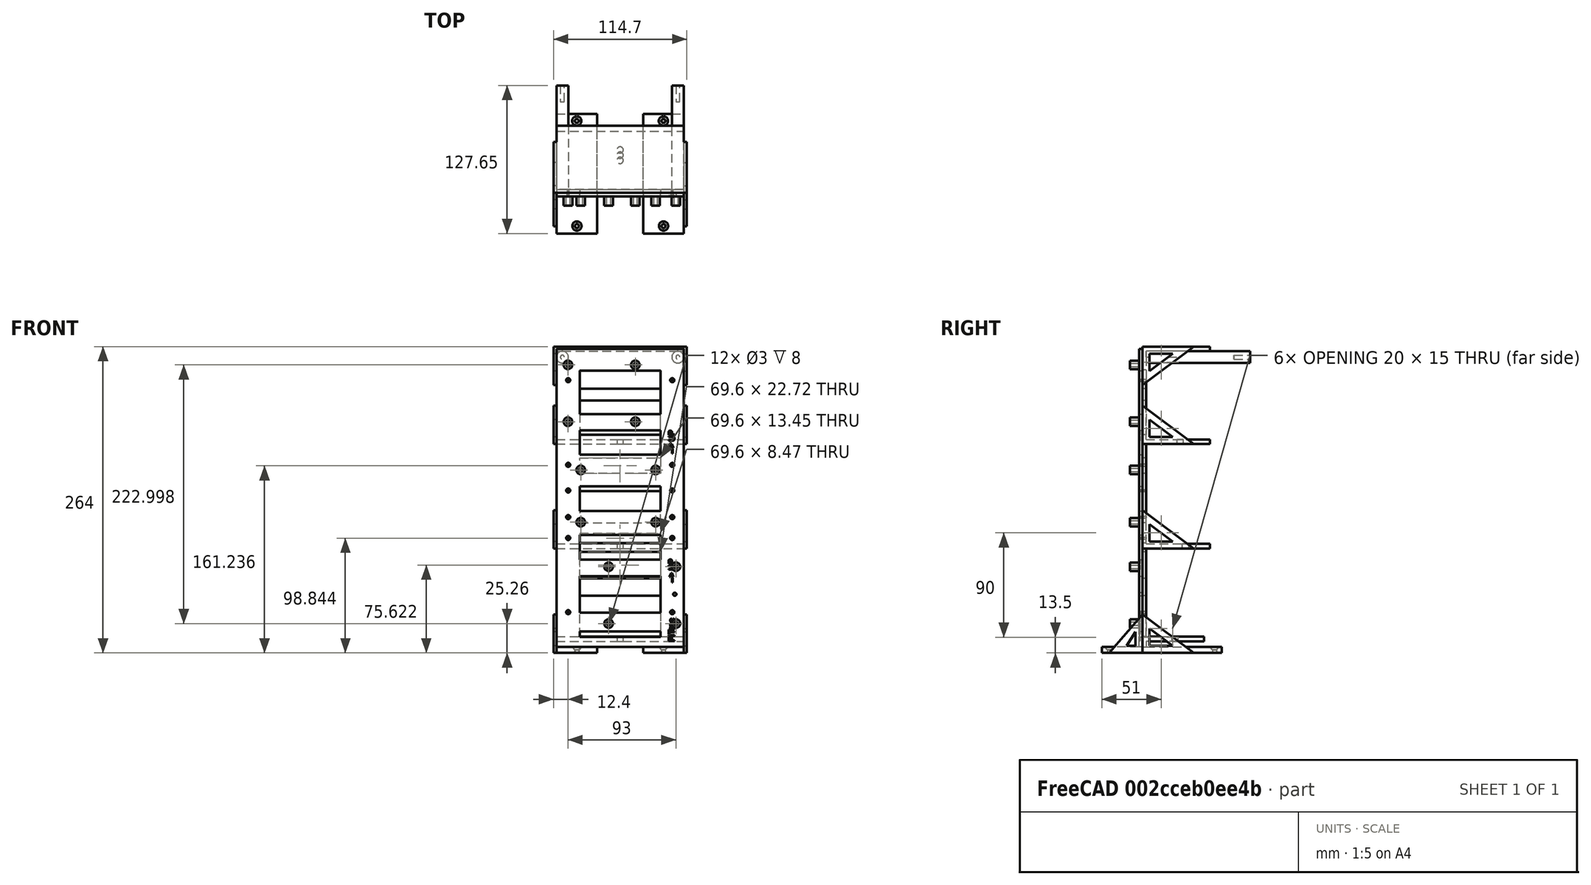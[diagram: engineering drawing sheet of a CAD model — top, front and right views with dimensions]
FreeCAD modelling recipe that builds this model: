
FCSTD DOCUMENT  (FreeCAD 1.0R39109 (Git))
Label: Tower
License: All rights reserved
LicenseURL: http://en.wikipedia.org/wiki/All_rights_reserved
objects: Sketcher::SketchObject×17, PartDesign::Pad×9, PartDesign::Plane×9, PartDesign::Pocket×5, PartDesign::Hole×3, PartDesign::Mirrored×2, PartDesign::Body×2, App::Link×1, Part::Part2DObjectPython×1, App::Part×1
note: 101 computed .brp shape members not serialized (recipe doc carries the construction recipe); baked Part::Feature solids carry a one-line shape summary decoded from their .brp
EXTERNAL_REF file=../Master Document.FCStd obj=Spreadsheet

FEATURE [App::Link] Link  label="Monitor Chassis Parameters"
  LinkedObject = -> <external ../Master Document.FCStd>#Spreadsheet
FEATURE [Sketcher::SketchObject] Sketch  label="Backplate Sketch"
  ArcFitTolerance = 1e-06
  AttachmentSupport = -> [XZ_Plane001]
  FullyConstrained = false
  MakeInternals = false
  MapMode = 5
  Placement = pos=(0,0,0) rot=(1,0,0;1.5708rad)
  expr: Constraints[10] = <<Monitor Chassis Parameters>>.GSBackPlateBoltDiameter
  expr: Constraints[11] = <<Monitor Chassis Parameters>>.GSComputeBoardWidth / 2 - <<Monitor Chassis Parameters>>.GSBackPlateOuterHolesInsetFromSide
  expr: Constraints[15] = <<Monitor Chassis Parameters>>.GSBackPlateWidthIncrement
  expr: Constraints[55] = <<Monitor Chassis Parameters>>.GSBackPlateLengthIncrement
  expr: Constraints[59] = <<Monitor Chassis Parameters>>.GSBackPlateWidth
  expr: Constraints[71] = <<Monitor Chassis Parameters>>.GSBackPlateMinimumSpanWidth
  expr: Constraints[72] = <<Monitor Chassis Parameters>>.GSBackPlateMinimumSpanWidth
  expr: Constraints[7] = <<Monitor Chassis Parameters>>.GSComputeBoardHeight
  expr: Constraints[80] = <<Monitor Chassis Parameters>>.GSBackPlateLengthIncrement
  expr: Constraints[8] = <<Monitor Chassis Parameters>>.GSComputeBoardWidth
  expr: Constraints[9] = <<Monitor Chassis Parameters>>.GSComputeBoardWidth / 2
  sketch-geometry (37):
    g0: LineSegment [constr] StartX=-50.8 StartY=24.4067 StartZ=0 EndX=50.8 EndY=24.4067 EndZ=0
    g1: LineSegment [constr] StartX=50.8 StartY=24.4067 StartZ=0 EndX=50.8 EndY=253.007 EndZ=0
    g2: LineSegment [constr] StartX=50.8 StartY=253.007 StartZ=0 EndX=-50.8 EndY=253.007 EndZ=0
    g3: LineSegment [constr] StartX=-50.8 StartY=253.007 StartZ=0 EndX=-50.8 EndY=24.4067 EndZ=0
    g4: Circle CenterX=46.99 CenterY=45.5 CenterZ=0 NormalX=0 NormalY=0 NormalZ=1 AngleXU=0 Radius=1.4
    g5: LineSegment StartX=-54.8 StartY=257.007 StartZ=0 EndX=-54.8 EndY=20.4067 EndZ=0
    g6: LineSegment [constr] StartX=-54.8 StartY=20.4067 StartZ=0 EndX=54.8 EndY=20.4067 EndZ=0
    g7: LineSegment StartX=34.8 StartY=117.208 StartZ=0 EndX=-34.8 EndY=117.208 EndZ=0
    g8: LineSegment StartX=-34.8 StartY=117.208 StartZ=0 EndX=-34.8 EndY=138.47 EndZ=0
    g9: LineSegment StartX=-34.8 StartY=138.47 StartZ=0 EndX=34.8 EndY=138.47 EndZ=0
    g10: LineSegment StartX=34.8 StartY=138.47 StartZ=0 EndX=34.8 EndY=117.208 EndZ=0
    g11: LineSegment StartX=34.8 StartY=238.176 StartZ=0 EndX=-34.8 EndY=238.176 EndZ=0
    g12: LineSegment StartX=-34.8 StartY=238.176 StartZ=0 EndX=-34.8 EndY=200.906 EndZ=0
    g13: LineSegment StartX=-34.8 StartY=200.906 StartZ=0 EndX=34.8 EndY=200.906 EndZ=0
    g14: LineSegment StartX=34.8 StartY=200.906 StartZ=0 EndX=34.8 EndY=238.176 EndZ=0
    g15: LineSegment StartX=-34.8 StartY=186.911 StartZ=0 EndX=-34.8 EndY=165.729 EndZ=0
    g16: LineSegment StartX=-34.8 StartY=165.729 StartZ=0 EndX=34.8 EndY=165.729 EndZ=0
    g17: LineSegment StartX=34.8 StartY=165.729 StartZ=0 EndX=34.8 EndY=186.911 EndZ=0
    g18: LineSegment StartX=34.8 StartY=186.911 StartZ=0 EndX=-34.8 EndY=186.911 EndZ=0
    g19: LineSegment StartX=-34.8 StartY=96.4911 StartZ=0 EndX=-34.8 EndY=75.4807 EndZ=0
    g20: LineSegment StartX=-34.8 StartY=75.4807 StartZ=0 EndX=34.8 EndY=75.4807 EndZ=0
    g21: LineSegment StartX=34.8 StartY=75.4807 StartZ=0 EndX=34.8 EndY=96.4911 EndZ=0
    g22: LineSegment StartX=34.8 StartY=96.4911 StartZ=0 EndX=-34.8 EndY=96.4911 EndZ=0
    g23: LineSegment StartX=-34.8 StartY=61.1974 StartZ=0 EndX=-34.8 EndY=29.6985 EndZ=0
    g24: LineSegment StartX=34.8 StartY=29.6985 StartZ=0 EndX=34.8 EndY=61.1974 EndZ=0
    g25: LineSegment StartX=54.8 StartY=20.4067 StartZ=0 EndX=54.8 EndY=257.007 EndZ=0
    g26: LineSegment StartX=-54.8 StartY=257.007 StartZ=0 EndX=54.8 EndY=257.007 EndZ=0
    g27: LineSegment StartX=-54.8 StartY=20.4067 StartZ=0 EndX=-54.8 EndY=0 EndZ=0
    g28: LineSegment StartX=-54.8 StartY=0 StartZ=0 EndX=54.8 EndY=0 EndZ=0
    g29: LineSegment StartX=54.8 StartY=0 StartZ=0 EndX=54.8 EndY=20.4067 EndZ=0
    g30: LineSegment [constr] StartX=54.8 StartY=20.4067 StartZ=0 EndX=-54.8 EndY=20.4067 EndZ=0
    g31: LineSegment StartX=-34.8 StartY=61.1974 StartZ=0 EndX=34.8 EndY=61.1974 EndZ=0
    g32: LineSegment StartX=-34.8 StartY=29.6985 StartZ=0 EndX=34.8 EndY=29.6985 EndZ=0
    g33: LineSegment StartX=-34.8 StartY=13.3729 StartZ=0 EndX=-34.8 EndY=8.79995 EndZ=0
    g34: LineSegment StartX=-34.8 StartY=8.79995 StartZ=0 EndX=34.8 EndY=8.79995 EndZ=0
    g35: LineSegment StartX=34.8 StartY=8.79995 StartZ=0 EndX=34.8 EndY=13.3729 EndZ=0
    g36: LineSegment StartX=34.8 StartY=13.3729 StartZ=0 EndX=-34.8 EndY=13.3729 EndZ=0
  constraints (96):
    c: Coincident(g0,g1)
    c: Coincident(g1,g2)
    c: Coincident(g2,g3)
    c: Coincident(g3,g0)
    c: Horizontal(g2)
    c: Vertical(g1)
    c: Vertical(g3)
    c: DistanceY(g0,g2) = 228.6
    c: DistanceX(g0,g0) = 101.6
    c: DistanceX(g0,g-1) = 50.8
    c: Diameter(g4) = 2.8
    c: DistanceX(g-1,g4) = 46.99
    c: Coincident(g5,g6)
    c: Vertical(g5)
    c: Horizontal(g6)
    c: DistanceX(g5,g0) = 4
    c: Horizontal(g0)
    c: Coincident(g7,g8)
    c: Coincident(g8,g9)
    c: Coincident(g9,g10)
    c: Coincident(g10,g7)
    c: Horizontal(g7)
    c: Vertical(g8)
    c: Vertical(g10)
    c: Coincident(g11,g12)
    c: Coincident(g12,g13)
    c: Coincident(g13,g14)
    c: Coincident(g14,g11)
    c: Horizontal(g11)
    c: Horizontal(g13)
    c: Vertical(g12)
    c: Vertical(g14)
    c: Coincident(g15,g16)
    c: Coincident(g16,g17)
    c: Coincident(g17,g18)
    c: Coincident(g18,g15)
    c: Vertical(g15)
    c: Vertical(g17)
    c: Horizontal(g16)
    c: Coincident(g19,g20)
    c: Coincident(g20,g21)
    c: Coincident(g21,g22)
    c: Coincident(g22,g19)
    c: Vertical(g19)
    c: Vertical(g21)
    c: Horizontal(g20)
    c: Horizontal(g22)
    c: Vertical(g23)
    c: Vertical(g24)
    c: Vertical(g15,g19)
    c: Vertical(g19,g23)
    c: Vertical(g7,g21)
    c: Vertical(g21,g24)
    c: Coincident(g25,g6)
    c: Vertical(g25)
    c: DistanceY(g1,g25) = 4
    c: Horizontal(g5,g25)
    c: Coincident(g26,g5)
    c: Coincident(g26,g25)
    c: DistanceX(g5,g6) = 109.6
    c: Coincident(g27,g28)
    c: Coincident(g28,g29)
    c: Coincident(g29,g30)
    c: Coincident(g30,g27)
    c: Vertical(g27)
    c: Vertical(g29)
    c: Horizontal(g28)
    c: Horizontal(g30)
    c: Coincident(g27,g5)
    c: Horizontal(g28,g-1)
    c: Vertical(g29,g6)
    c: DistanceX(g5,g11) = 20
    c: DistanceX(g11,g25) = 20
    c: Horizontal(g9)
    c: Coincident(g31,g23)
    c: Coincident(g31,g24)
    c: Horizontal(g31)
    c: Vertical(g11,g15)
    c: Vertical(g11,g9)
    c: Vertical(g16,g9)
    c: DistanceY(g5,g0) = 4
    c: Coincident(g32,g23)
    c: Coincident(g32,g24)
    c: Horizontal(g32)
    c: Horizontal(g18)
    c: Vertical(g15,g8)
    c: Coincident(g33,g34)
    c: Coincident(g34,g35)
    c: Coincident(g35,g36)
    c: Coincident(g36,g33)
    c: Vertical(g33)
    c: Vertical(g35)
    c: Horizontal(g34)
    c: Horizontal(g36)
    c: Vertical(g23,g33)
    c: Vertical(g24,g35)
FEATURE [PartDesign::Pad] Pad  label="Backplate Pad"
  Direction = (0,-1,2e-16)
  Length = 3
  Length2 = 10
  Placement = pos=(0,0,0) rot=(1,0,0;1.5708rad)
  Profile = -> Sketch
  ReferenceAxis = -> Sketch [N_Axis]
  Reversed = true
  Suppressed = false
  Type = 0
  expr: Length = <<Monitor Chassis Parameters>>.GSBackPlateThickness
FEATURE [Sketcher::SketchObject] Sketch001  label="Backplate Risers Sketch"
  ArcFitTolerance = 1e-06
  AttachmentSupport = -> [XZ_Plane001]
  FullyConstrained = false
  MakeInternals = false
  MapMode = 5
  Placement = pos=(0,0,0) rot=(1,0,0;1.5708rad)
  expr: Constraints[10] = <<Monitor Chassis Parameters>>.GsPi5MountingHoleDiameter
  expr: Constraints[11] = <<Monitor Chassis Parameters>>.GsPi5MountingHoleDiameter
  expr: Constraints[12] = <<Monitor Chassis Parameters>>.GsPi5MountingHoleDiameter
  expr: Constraints[13] = <<Monitor Chassis Parameters>>.GsPi5MountingHoleDiameter
  expr: Constraints[17] = <<Monitor Chassis Parameters>>.GSBackPlateScrewHoleDiameter + 2 * <<Monitor Chassis Parameters>>.GSBackPlateStandoffWallThickness
  expr: Constraints[19] = <<Monitor Chassis Parameters>>.GSBackPlateScrewHoleDiameter + 2 * <<Monitor Chassis Parameters>>.GSBackPlateStandoffWallThickness
  expr: Constraints[25] = <<Monitor Chassis Parameters>>.GSBackPlateScrewHoleDiameter + 2 * <<Monitor Chassis Parameters>>.GSBackPlateStandoffWallThickness
  expr: Constraints[26] = <<Monitor Chassis Parameters>>.GSBackPlateScrewHoleDiameter + 2 * <<Monitor Chassis Parameters>>.GSBackPlateStandoffWallThickness
  expr: Constraints[27] = <<Monitor Chassis Parameters>>.GSBackPlateScrewHoleDiameter + 2 * <<Monitor Chassis Parameters>>.GSBackPlateStandoffWallThickness
  expr: Constraints[28] = <<Monitor Chassis Parameters>>.GSBackPlateScrewHoleDiameter + 2 * <<Monitor Chassis Parameters>>.GSBackPlateStandoffWallThickness
  expr: Constraints[29] = <<Monitor Chassis Parameters>>.GSBackPlateScrewHoleDiameter + 2 * <<Monitor Chassis Parameters>>.GSBackPlateStandoffWallThickness
  expr: Constraints[31] = <<Monitor Chassis Parameters>>.GSBackPlateVerticalOffset
  expr: Constraints[33] = <<Monitor Chassis Parameters>>.GSPi5MountingHoleCenterLength
  expr: Constraints[35] = <<Monitor Chassis Parameters>>.GSPi5MountingHoleCenterWidth
  expr: Constraints[37] = <<Monitor Chassis Parameters>>.GSPi5MountingHoleCenterWidth
  expr: Constraints[40] = <<Monitor Chassis Parameters>>.GsPi5MountingHoleDiameter
  expr: Constraints[57] = <<Monitor Chassis Parameters>>.GSMonitorConnectorBoardHoleSeparationLength
  expr: Constraints[58] = <<Monitor Chassis Parameters>>.GSMonitorConnectorBoardHoleSeparationWidth
  expr: Constraints[59] = 34
  expr: Constraints[60] = <<Monitor Chassis Parameters>>.GSPi5MountingHoleCenterLength
  expr: Constraints[61] = 10
  expr: Constraints[6] = <<Monitor Chassis Parameters>>.GSComputeBoardWidth / 2
  expr: Constraints[7] = <<Monitor Chassis Parameters>>.GsPi5MountingHoleDiameter
  expr: Constraints[8] = <<Monitor Chassis Parameters>>.GsPi5MountingHoleDiameter
  expr: Constraints[9] = <<Monitor Chassis Parameters>>.GsPi5MountingHoleDiameter
  sketch-geometry (28):
    g0: LineSegment [constr] StartX=-50.8 StartY=20 StartZ=0 EndX=50.8 EndY=20 EndZ=0
    g1: LineSegment [constr] StartX=50.8 StartY=20 StartZ=0 EndX=50.8 EndY=248.6 EndZ=0
    g2: LineSegment [constr] StartX=50.8 StartY=248.6 StartZ=0 EndX=-50.8 EndY=248.6 EndZ=0
    g3: LineSegment [constr] StartX=-50.8 StartY=248.6 StartZ=0 EndX=-50.8 EndY=20 EndZ=0
    g4: Circle CenterX=-45 CenterY=243.258 CenterZ=0 NormalX=0 NormalY=0 NormalZ=1 AngleXU=0 Radius=1.5
    g5: Circle CenterX=13 CenterY=243.258 CenterZ=0 NormalX=0 NormalY=0 NormalZ=1 AngleXU=0 Radius=1.5
    g6: Circle CenterX=-10 CenterY=20.2601 CenterZ=0 NormalX=0 NormalY=0 NormalZ=1 AngleXU=0 Radius=1.5
    g7: Circle CenterX=48 CenterY=20.2601 CenterZ=0 NormalX=0 NormalY=0 NormalZ=1 AngleXU=0 Radius=1.5
    g8: Circle CenterX=-10 CenterY=69.2601 CenterZ=0 NormalX=0 NormalY=0 NormalZ=1 AngleXU=0 Radius=1.5
    g9: Circle CenterX=-45 CenterY=194.258 CenterZ=0 NormalX=0 NormalY=0 NormalZ=1 AngleXU=0 Radius=1.5
    g10: Circle CenterX=13 CenterY=194.258 CenterZ=0 NormalX=0 NormalY=0 NormalZ=1 AngleXU=0 Radius=1.5
    g11: Circle CenterX=-45 CenterY=243.258 CenterZ=0 NormalX=0 NormalY=0 NormalZ=1 AngleXU=0 Radius=3.7
    g12: Circle CenterX=13 CenterY=243.258 CenterZ=0 NormalX=0 NormalY=0 NormalZ=1 AngleXU=0 Radius=3.7
    g13: Circle CenterX=-45 CenterY=194.258 CenterZ=0 NormalX=0 NormalY=0 NormalZ=1 AngleXU=0 Radius=3.7
    g14: Circle CenterX=13 CenterY=194.258 CenterZ=0 NormalX=0 NormalY=0 NormalZ=1 AngleXU=0 Radius=3.7
    g15: Circle CenterX=-10 CenterY=69.2601 CenterZ=0 NormalX=0 NormalY=0 NormalZ=1 AngleXU=0 Radius=3.7
    g16: Circle CenterX=-10 CenterY=20.2601 CenterZ=0 NormalX=0 NormalY=0 NormalZ=1 AngleXU=0 Radius=3.7
    g17: Circle CenterX=48 CenterY=20.2601 CenterZ=0 NormalX=0 NormalY=0 NormalZ=1 AngleXU=0 Radius=3.7
    g18: Circle CenterX=48 CenterY=69.2601 CenterZ=0 NormalX=0 NormalY=0 NormalZ=1 AngleXU=0 Radius=3.7
    g19: Circle CenterX=48 CenterY=69.2601 CenterZ=0 NormalX=0 NormalY=0 NormalZ=1 AngleXU=0 Radius=1.5
    g20: Circle CenterX=-34 CenterY=107.639 CenterZ=0 NormalX=0 NormalY=0 NormalZ=1 AngleXU=0 Radius=1.5
    g21: Circle CenterX=-34 CenterY=107.639 CenterZ=0 NormalX=0 NormalY=0 NormalZ=1 AngleXU=0 Radius=3.7
    g22: Circle CenterX=30.5 CenterY=107.639 CenterZ=0 NormalX=0 NormalY=0 NormalZ=1 AngleXU=0 Radius=1.5
    g23: Circle CenterX=30.5 CenterY=107.639 CenterZ=0 NormalX=0 NormalY=0 NormalZ=1 AngleXU=0 Radius=3.7
    g24: Circle CenterX=30.5 CenterY=152.639 CenterZ=0 NormalX=0 NormalY=0 NormalZ=1 AngleXU=0 Radius=1.5
    g25: Circle CenterX=30.5 CenterY=152.639 CenterZ=0 NormalX=0 NormalY=0 NormalZ=1 AngleXU=0 Radius=3.7
    g26: Circle CenterX=-34 CenterY=152.639 CenterZ=0 NormalX=0 NormalY=0 NormalZ=1 AngleXU=0 Radius=1.5
    g27: Circle CenterX=-34 CenterY=152.639 CenterZ=0 NormalX=0 NormalY=0 NormalZ=1 AngleXU=0 Radius=3.7
  constraints (67):
    c: Coincident(g0,g1)
    c: Coincident(g1,g2)
    c: Coincident(g2,g3)
    c: Coincident(g3,g0)
    c: Vertical(g1)
    c: Vertical(g3)
    c: DistanceX(g0,g-1) = 50.8
    c: Diameter(g4) = 3
    c: Diameter(g5) = 3
    c: Diameter(g6) = 3
    c: Diameter(g7) = 3
    c: Diameter(g8) = 3
    c: Diameter(g9) = 3
    c: Diameter(g10) = 3
    c: Horizontal(g0)
    c: Horizontal(g5,g4)
    c: Coincident(g11,g4)
    c: Diameter(g11) = 7.4
    c: Coincident(g12,g5)
    c: Diameter(g12) = 7.4
    c: Coincident(g13,g9)
    c: Coincident(g14,g10)
    c: Coincident(g15,g8)
    c: Coincident(g16,g6)
    c: Coincident(g17,g7)
    c: Diameter(g17) = 7.4
    c: Diameter(g16) = 7.4
    c: Diameter(g15) = 7.4
    c: Diameter(g14) = 7.4
    c: Diameter(g13) = 7.4
    c: Horizontal(g7,g6)
    c: DistanceY(g-1,g0) = 20
    c: Horizontal(g2,g1)
    c: DistanceX(g4,g5) = 58
    c: Horizontal(g9,g10)
    c: DistanceY(g9,g4) = 49
    c: Vertical(g8,g6)
    c: DistanceY(g6,g8) = 49
    c: Diameter(g18) = 7.4
    c: Coincident(g19,g18)
    c: Diameter(g19) = 3
    c: Horizontal(g18,g8)
    c: Vertical(g18,g7)
    c: Coincident(g21,g20)
    c: Diameter(g21) = 7.4
    c: Diameter(g20) = 3
    c: Coincident(g23,g22)
    c: Diameter(g23) = 7.4
    c: Diameter(g22) = 3
    c: Coincident(g25,g24)
    c: Diameter(g25) = 7.4
    c: Diameter(g24) = 3
    c: Coincident(g27,g26)
    c: Diameter(g27) = 7.4
    c: Diameter(g26) = 3
    c: Horizontal(g24,g26)
    c: Horizontal(g22,g20)
    c: DistanceX(g26,g24) = 64.5
    c: DistanceY(g20,g26) = 45
    c: DistanceX(g26,g-1) = 34
    c: DistanceX(g8,g18) = 58
    c: DistanceX(g6,g-1) = 10
    c: DistanceX(g9,g-1) = 45
    c: Vertical(g5,g10)
    c: Vertical(g4,g9)
    c: Vertical(g20,g26)
    c: Vertical(g24,g22)
FEATURE [PartDesign::Pad] Pad001  label="Backplate Risers Pad"
  BaseFeature = -> Pad
  Direction = (0,-1,2e-16)
  Length = 8
  Length2 = 10
  Placement = pos=(0,0,0) rot=(1,0,0;1.5708rad)
  Profile = -> Sketch001
  ReferenceAxis = -> Sketch001 [N_Axis]
  Suppressed = false
  Type = 0
  expr: Length = <<Monitor Chassis Parameters>>.GSBackPlateConnectorBoardVariantStandoffHeight
FEATURE [Sketcher::SketchObject] Sketch002  label="Backplate Foot Sketch"
  ArcFitTolerance = 1e-06
  AttachmentSupport = -> [XZ_Plane001]
  FullyConstrained = true
  MakeInternals = false
  MapMode = 5
  Placement = pos=(0,0,0) rot=(1,0,0;1.5708rad)
  expr: Constraints[11] = <<Monitor Chassis Parameters>>.GSTowerFeetThickness
  expr: Constraints[21] = <<Monitor Chassis Parameters>>.GSTowerFeetThickness
  expr: Constraints[22] = <<Monitor Chassis Parameters>>.GSBackPlateFootWidth
  expr: Constraints[23] = 0.5 * <<Monitor Chassis Parameters>>.GSBackPlateWidth
  expr: Constraints[8] = <<Monitor Chassis Parameters>>.GSBackPlateFootWidth
  expr: Constraints[9] = 0.5 * <<Monitor Chassis Parameters>>.GSBackPlateWidth
  sketch-geometry (8):
    g0: LineSegment StartX=-54.8 StartY=-5 StartZ=0 EndX=-19.8 EndY=-5 EndZ=0
    g1: LineSegment StartX=-19.8 StartY=-5 StartZ=0 EndX=-19.8 EndY=0 EndZ=0
    g2: LineSegment StartX=-19.8 StartY=0 StartZ=0 EndX=-54.8 EndY=0 EndZ=0
    g3: LineSegment StartX=-54.8 StartY=0 StartZ=0 EndX=-54.8 EndY=-5 EndZ=0
    g4: LineSegment StartX=54.8 StartY=-5 StartZ=0 EndX=54.8 EndY=0 EndZ=0
    g5: LineSegment StartX=54.8 StartY=0 StartZ=0 EndX=19.8 EndY=0 EndZ=0
    g6: LineSegment StartX=19.8 StartY=0 StartZ=0 EndX=19.8 EndY=-5 EndZ=0
    g7: LineSegment StartX=19.8 StartY=-5 StartZ=0 EndX=54.8 EndY=-5 EndZ=0
  constraints (24):
    c: Coincident(g0,g1)
    c: Coincident(g1,g2)
    c: Coincident(g2,g3)
    c: Coincident(g3,g0)
    c: Horizontal(g0)
    c: Horizontal(g2)
    c: Vertical(g1)
    c: Vertical(g3)
    c: DistanceX(g2,g1) = 35
    c: DistanceX(g2,g-1) = 54.8
    c: Horizontal(g2,g-1)
    c: DistanceY(g0,g2) = 5
    c: Coincident(g4,g5)
    c: Coincident(g5,g6)
    c: Coincident(g6,g7)
    c: Coincident(g7,g4)
    c: Vertical(g4)
    c: Vertical(g6)
    c: Horizontal(g5)
    c: Horizontal(g7)
    c: Horizontal(g5,g-1)
    c: DistanceY(g4,g4) = 5
    c: DistanceX(g6,g4) = 35
    c: DistanceX(g-1,g4) = 54.8
FEATURE [PartDesign::Pad] Pad002  label="Backplate Foot Pad"
  BaseFeature = -> Pad001
  Direction = (0,-1,2e-16)
  Length = 32
  Length2 = 3
  Placement = pos=(0,0,0) rot=(1,0,0;1.5708rad)
  Profile = -> Sketch002
  ReferenceAxis = -> Sketch002 [N_Axis]
  Suppressed = false
  Type = 4
  expr: Length = <<Monitor Chassis Parameters>>.GSBackPlateFootLengthBackward
  expr: Length2 = <<Monitor Chassis Parameters>>.GSBackPlateThickness
FEATURE [Sketcher::SketchObject] Sketch003  label="Backplate Foot Screw Holes Sketch"
  ArcFitTolerance = 1e-06
  AttachmentSupport = -> [XY_Plane001]
  FullyConstrained = true
  MakeInternals = false
  MapMode = 5
  expr: Constraints[0] = 0.8 * <<Monitor Chassis Parameters>>.GSBackPlateFootLengthBackward
  expr: Constraints[1] = 0.5 * <<Monitor Chassis Parameters>>.GSBackPlateWidth - 0.5 * <<Monitor Chassis Parameters>>.GSBackPlateFootWidth
  expr: Constraints[2] = 0.5 * <<Monitor Chassis Parameters>>.GSBackPlateWidth - 0.5 * <<Monitor Chassis Parameters>>.GSBackPlateFootWidth
  expr: Constraints[3] = <<Monitor Chassis Parameters>>.GSTowerFeetScrewDiameter
  expr: Constraints[4] = <<Monitor Chassis Parameters>>.GSTowerFeetScrewDiameter
  sketch-geometry (2):
    g0: Circle CenterX=-37.3 CenterY=-25.6 CenterZ=0 NormalX=0 NormalY=0 NormalZ=1 AngleXU=0 Radius=1.7
    g1: Circle CenterX=37.3 CenterY=-25.6 CenterZ=0 NormalX=0 NormalY=0 NormalZ=1 AngleXU=0 Radius=1.7
  constraints (6):
    c: DistanceY(g0,g-1) = 25.6
    c: DistanceX(g0,g-1) = 37.3
    c: DistanceX(g-1,g1) = 37.3
    c: Diameter(g0) = 3.4
    c: Diameter(g1) = 3.4
    c: Horizontal(g1,g0)
FEATURE [PartDesign::Hole] Hole  label="Backplate Foot Screw Holes"
  BaseFeature = -> Pad002
  CustomThreadClearance = 0
  Depth = 25
  DepthType = 0
  Diameter = 3.4
  DrillForDepth = false
  DrillPoint = 1
  DrillPointAngle = 118
  HoleCutCountersinkAngle = 90
  HoleCutCustomValues = false
  HoleCutDepth = 0
  HoleCutDiameter = 8
  HoleCutType = 2
  ModelThread = false
  Placement = pos=(0,0,0) rot=(1,0,0;1.5708rad)
  Profile = -> Sketch003
  Suppressed = false
  Tapered = false
  TaperedAngle = 90
  ThreadClass = 0
  ThreadDepth = 25
  ThreadDepthType = 0
  ThreadDirection = 0
  ThreadFit = 0
  ThreadSize = 0
  ThreadType = 0
  Threaded = false
  UseCustomThreadClearance = false
  expr: Diameter = <<Monitor Chassis Parameters>>.GSTowerFeetScrewDiameter
  expr: HoleCutDiameter = <<Monitor Chassis Parameters>>.GSM4BoltCountersinkDiameter
FEATURE [PartDesign::Plane] DatumPlane
  AttachmentOffset = pos=(0,0,54.8) rot=(0,0,1;0rad)
  AttachmentSupport = -> [YZ_Plane001]
  Length = 76.5738
  MapMode = 5
  Placement = pos=(54.8,0,0) rot=(0.57735,0.57735,0.57735;2.0944rad)
  ResizeMode = 0
  Width = 306.293
  expr: .AttachmentOffset.Base.z = 0.5 * <<Monitor Chassis Parameters>>.GSBackPlateWidth
FEATURE [Sketcher::SketchObject] Sketch004  label="Foot Support Corner Sketch"
  ArcFitTolerance = 1e-06
  AttachmentSupport = -> [DatumPlane]
  FullyConstrained = true
  MakeInternals = false
  MapMode = 5
  Placement = pos=(54.8,0,0) rot=(0.57735,0.57735,0.57735;2.0944rad)
  expr: Constraints[14] = <<Monitor Chassis Parameters>>.GSSideCornerCutoutInset
  expr: Constraints[15] = <<Monitor Chassis Parameters>>.GSSideCornerCutoutInset
  expr: Constraints[16] = 2.5 * <<Monitor Chassis Parameters>>.GSSideCornerCutoutInset
  expr: Constraints[17] = 2.5 * <<Monitor Chassis Parameters>>.GSSideCornerCutoutInset
  expr: Constraints[1] = <<Monitor Chassis Parameters>>.GSBackPlateThickness
  expr: Constraints[4] = <<Monitor Chassis Parameters>>.GSTowerFeetThickness
  expr: Constraints[7] = 0.9 * <<Monitor Chassis Parameters>>.GSBackPlateFootLengthBackward
  expr: Constraints[8] = 0.6 * <<Monitor Chassis Parameters>>.GSTowerFloorDepth
  sketch-geometry (6):
    g0: LineSegment StartX=-25.8 StartY=-5 StartZ=0 EndX=3 EndY=-5 EndZ=0
    g1: LineSegment StartX=3 StartY=28 StartZ=0 EndX=3 EndY=-5 EndZ=0
    g2: LineSegment StartX=-25.8 StartY=-5 StartZ=0 EndX=3 EndY=28 EndZ=0
    g3: LineSegment StartX=-10.8 StartY=1 StartZ=0 EndX=-3 EndY=13 EndZ=0
    g4: LineSegment StartX=-3 StartY=13 StartZ=0 EndX=-3 EndY=1 EndZ=0
    g5: LineSegment StartX=-10.8 StartY=1 StartZ=0 EndX=-3 EndY=1 EndZ=0
  constraints (18):
    c: Horizontal(g0)
    c: DistanceX(g-1,g0) = 3
    c: Coincident(g1,g0)
    c: Vertical(g1)
    c: DistanceY(g0,g-1) = 5
    c: Coincident(g2,g0)
    c: Coincident(g2,g1)
    c: DistanceX(g0,g0) = 28.8
    c: DistanceY(g0,g1) = 33
    c: Coincident(g4,g3)
    c: Vertical(g4)
    c: Coincident(g5,g3)
    c: Coincident(g5,g4)
    c: Horizontal(g5)
    c: DistanceY(g0,g4) = 6
    c: DistanceX(g4,g0) = 6
    c: DistanceX(g0,g3) = 15
    c: DistanceY(g3,g1) = 15
FEATURE [PartDesign::Pad] Pad003  label="Foot Support Corner Pad"
  BaseFeature = -> Hole
  Direction = (1,0,0)
  Length = 2.5
  Length2 = 10
  Placement = pos=(0,0,0) rot=(1,0,0;1.5708rad)
  Profile = -> Sketch004
  ReferenceAxis = -> Sketch004 [N_Axis]
  Suppressed = false
  Type = 0
  expr: Length = <<Monitor Chassis Parameters>>.GSSideCornerThickness
FEATURE [PartDesign::Mirrored] Mirrored  label="Foot Support Corner Mirrored"
  BaseFeature = -> Pad003
  MirrorPlane = -> YZ_Plane001
  Originals = -> [Pad003]
  Placement = pos=(0,0,0) rot=(1,0,0;1.5708rad)
  Suppressed = false
  TransformMode = 0
FEATURE [PartDesign::Plane] DatumPlane001
  AttachmentOffset = pos=(0,0,54.8) rot=(0,0,1;0rad)
  AttachmentSupport = -> [YZ_Plane002]
  Length = 121.975
  MapMode = 5
  Placement = pos=(54.8,0,0) rot=(0.57735,0.57735,0.57735;2.0944rad)
  ResizeMode = 0
  Width = 315.975
  expr: .AttachmentOffset.Base.z = 0.5 * <<Monitor Chassis Parameters>>.GSBackPlateWidth
FEATURE [Sketcher::SketchObject] Sketch005  label="Frontplate Sketch"
  ArcFitTolerance = 1e-06
  AttachmentSupport = -> [XZ_Plane002]
  FullyConstrained = false
  MakeInternals = false
  MapMode = 5
  Placement = pos=(0,0,0) rot=(1,0,0;1.5708rad)
  expr: Constraints[105] = <<Monitor Chassis Parameters>>.GSFrontPlateMinimumSpanWidth - 5
  expr: Constraints[106] = <<Monitor Chassis Parameters>>.GSTowerFourthFloorHeight + <<Monitor Chassis Parameters>>.GSTowerFloorThickness
  expr: Constraints[107] = <<Monitor Chassis Parameters>>.GSTowerLayerJoinScrewDiameter
  expr: Constraints[108] = <<Monitor Chassis Parameters>>.GSTowerLayerJoinScrewDiameter
  expr: Constraints[110] = <<Monitor Chassis Parameters>>.GSTowerLayerJoinScrewInset
  expr: Constraints[111] = <<Monitor Chassis Parameters>>.GSTowerLayerJoinScrewInset
  expr: Constraints[112] = <<Monitor Chassis Parameters>>.GSTowerLayerJoinScrewDiameter
  expr: Constraints[113] = <<Monitor Chassis Parameters>>.GSTowerLayerJoinScrewDiameter
  expr: Constraints[115] = <<Monitor Chassis Parameters>>.GSTowerLayerJoinScrewDiameter
  expr: Constraints[116] = <<Monitor Chassis Parameters>>.GSTowerLayerJoinScrewDiameter
  expr: Constraints[120] = <<Monitor Chassis Parameters>>.GSTowerLayerJoinScrewDiameter
  expr: Constraints[121] = <<Monitor Chassis Parameters>>.GSTowerLayerJoinScrewDiameter
  expr: Constraints[123] = <<Monitor Chassis Parameters>>.GSTowerLayerJoinScrewHeightFromFoot_1
  expr: Constraints[124] = <<Monitor Chassis Parameters>>.GSTowerLayerJoinScrewHeightFromFoot_3
  expr: Constraints[126] = <<Monitor Chassis Parameters>>.GSTowerLayerJoinScrewHeightFromFoot_4
  expr: Constraints[127] = <<Monitor Chassis Parameters>>.GSTowerLayerJoinScrewHeightFromFoot_5
  expr: Constraints[129] = <<Monitor Chassis Parameters>>.GSTowerLayerJoinScrewDiameter
  expr: Constraints[130] = <<Monitor Chassis Parameters>>.GSTowerLayerJoinScrewDiameter
  expr: Constraints[133] = <<Monitor Chassis Parameters>>.GSTowerLayerJoinScrewHeightFromFoot_6
  expr: Constraints[13] = <<Monitor Chassis Parameters>>.GSBackPlateWidthIncrement
  expr: Constraints[145] = <<Monitor Chassis Parameters>>.GSTowerLayerJoinScrewDiameter
  expr: Constraints[150] = <<Monitor Chassis Parameters>>.GSTowerLayerJoinScrewHeightFromFoot_2
  expr: Constraints[46] = <<Monitor Chassis Parameters>>.GSFrontPlateMinimumSpanWidth - 10
  expr: Constraints[48] = <<Monitor Chassis Parameters>>.GSFrontPlateMinimumSpanWidth
  expr: Constraints[65] = <<Monitor Chassis Parameters>>.GSFrontPlateMinimumSpanWidth - 5
  expr: Constraints[71] = <<Monitor Chassis Parameters>>.GSBackPlateLengthIncrement
  expr: Constraints[75] = <<Monitor Chassis Parameters>>.GSBackPlateWidth
  expr: Constraints[76] = <<Monitor Chassis Parameters>>.GSBackPlateVerticalOffset
  expr: Constraints[7] = <<Monitor Chassis Parameters>>.GSComputeBoardHeight
  expr: Constraints[8] = <<Monitor Chassis Parameters>>.GSComputeBoardWidth
  expr: Constraints[96] = <<Monitor Chassis Parameters>>.GSFrontPlateMinimumSpanWidth - 11
  expr: Constraints[97] = <<Monitor Chassis Parameters>>.GSFrontPlateMinimumSpanWidth
  expr: Constraints[98] = <<Monitor Chassis Parameters>>.GSFrontPlateMinimumSpanWidth
  expr: Constraints[9] = <<Monitor Chassis Parameters>>.GSComputeBoardWidth / 2
  sketch-geometry (55):
    g0: LineSegment [constr] StartX=-50.8 StartY=24 StartZ=0 EndX=50.8 EndY=24 EndZ=0
    g1: LineSegment [constr] StartX=50.8 StartY=24 StartZ=0 EndX=50.8 EndY=252.6 EndZ=0
    g2: LineSegment [constr] StartX=50.8 StartY=252.6 StartZ=0 EndX=-50.8 EndY=252.6 EndZ=0
    g3: LineSegment [constr] StartX=-50.8 StartY=252.6 StartZ=0 EndX=-50.8 EndY=24 EndZ=0
    g4: LineSegment StartX=-54.8 StartY=256.6 StartZ=0 EndX=-54.8 EndY=20 EndZ=0
    g5: LineSegment [constr] StartX=-54.8 StartY=20 StartZ=0 EndX=54.8 EndY=20 EndZ=0
    g6: LineSegment StartX=34.8 StartY=162.959 StartZ=0 EndX=-34.8 EndY=162.959 EndZ=0
    g7: LineSegment StartX=-34.8 StartY=162.959 StartZ=0 EndX=-34.8 EndY=149.512 EndZ=0
    g8: LineSegment StartX=-34.8 StartY=149.512 StartZ=0 EndX=34.8 EndY=149.512 EndZ=0
    g9: LineSegment StartX=34.8 StartY=149.512 StartZ=0 EndX=34.8 EndY=162.959 EndZ=0
    g10: LineSegment StartX=34.8 StartY=107.062 StartZ=0 EndX=-34.8 EndY=107.062 EndZ=0
    g11: LineSegment StartX=-34.8 StartY=107.062 StartZ=0 EndX=-34.8 EndY=134.512 EndZ=0
    g12: LineSegment StartX=-34.8 StartY=134.512 StartZ=0 EndX=34.8 EndY=134.512 EndZ=0
    g13: LineSegment StartX=34.8 StartY=134.512 StartZ=0 EndX=34.8 EndY=107.062 EndZ=0
    g14: LineSegment StartX=34.8 StartY=239 StartZ=0 EndX=-34.8 EndY=239 EndZ=0
    g15: LineSegment StartX=-34.8 StartY=239 StartZ=0 EndX=-34.8 EndY=222.58 EndZ=0
    g16: LineSegment StartX=-34.8 StartY=222.58 StartZ=0 EndX=34.8 EndY=222.58 EndZ=0
    g17: LineSegment StartX=34.8 StartY=222.58 StartZ=0 EndX=34.8 EndY=239 EndZ=0
    g18: LineSegment StartX=34.8 StartY=182.959 StartZ=0 EndX=-34.8 EndY=182.959 EndZ=0
    g19: LineSegment StartX=-34.8 StartY=182.959 StartZ=0 EndX=-34.8 EndY=212.58 EndZ=0
    g20: LineSegment StartX=-34.8 StartY=212.58 StartZ=0 EndX=34.8 EndY=212.58 EndZ=0
    g21: LineSegment StartX=34.8 StartY=212.58 StartZ=0 EndX=34.8 EndY=182.959 EndZ=0
    g22: LineSegment StartX=-34.8 StartY=81.9803 StartZ=0 EndX=-34.8 EndY=59.2632 EndZ=0
    g23: LineSegment StartX=-34.8 StartY=59.2632 StartZ=0 EndX=34.8 EndY=59.2632 EndZ=0
    g24: LineSegment StartX=34.8 StartY=59.2632 StartZ=0 EndX=34.8 EndY=81.9803 EndZ=0
    g25: LineSegment StartX=34.8 StartY=81.9803 StartZ=0 EndX=-34.8 EndY=81.9803 EndZ=0
    g26: LineSegment StartX=-34.8 StartY=44.2632 StartZ=0 EndX=-34.8 EndY=9 EndZ=0
    g27: LineSegment StartX=-34.8 StartY=9 StartZ=0 EndX=34.8 EndY=9 EndZ=0
    g28: LineSegment StartX=34.8 StartY=9 StartZ=0 EndX=34.8 EndY=44.2632 EndZ=0
    g29: LineSegment StartX=34.8 StartY=44.2632 StartZ=0 EndX=-34.8 EndY=44.2632 EndZ=0
    g30: LineSegment StartX=54.8 StartY=20 StartZ=0 EndX=54.8 EndY=256.6 EndZ=0
    g31: LineSegment [constr] StartX=-54.8 StartY=256.6 StartZ=0 EndX=54.8 EndY=256.6 EndZ=0
    g32: LineSegment StartX=-54.8 StartY=20 StartZ=0 EndX=-54.8 EndY=0 EndZ=0
    g33: LineSegment StartX=-54.8 StartY=0 StartZ=0 EndX=54.8 EndY=0 EndZ=0
    g34: LineSegment StartX=54.8 StartY=0 StartZ=0 EndX=54.8 EndY=20 EndZ=0
    g35: LineSegment [constr] StartX=54.8 StartY=20 StartZ=0 EndX=-54.8 EndY=20 EndZ=0
    g36: LineSegment StartX=-54.8 StartY=256.6 StartZ=0 EndX=-54.8 EndY=259 EndZ=0
    g37: LineSegment StartX=-54.8 StartY=259 StartZ=0 EndX=54.8 EndY=259 EndZ=0
    g38: LineSegment StartX=54.8 StartY=259 StartZ=0 EndX=54.8 EndY=256.6 EndZ=0
    g39: Circle CenterX=-44.8 CenterY=30 CenterZ=0 NormalX=0 NormalY=0 NormalZ=1 AngleXU=0 Radius=0.855
    g40: Circle CenterX=44.8 CenterY=30 CenterZ=0 NormalX=0 NormalY=0 NormalZ=1 AngleXU=0 Radius=0.855
    g41: Circle CenterX=-44.8 CenterY=112 CenterZ=0 NormalX=0 NormalY=0 NormalZ=1 AngleXU=0 Radius=0.855
    g42: Circle CenterX=44.8 CenterY=112 CenterZ=0 NormalX=0 NormalY=0 NormalZ=1 AngleXU=0 Radius=0.855
    g43: Circle CenterX=-44.8 CenterY=157 CenterZ=0 NormalX=0 NormalY=0 NormalZ=1 AngleXU=0 Radius=0.855
    g44: Circle CenterX=44.8 CenterY=157 CenterZ=0 NormalX=0 NormalY=0 NormalZ=1 AngleXU=0 Radius=0.855
    g45: Circle CenterX=-44.8 CenterY=135 CenterZ=0 NormalX=0 NormalY=0 NormalZ=1 AngleXU=0 Radius=0.855
    g46: Circle CenterX=44.8 CenterY=135 CenterZ=0 NormalX=0 NormalY=0 NormalZ=1 AngleXU=0 Radius=0.855
    g47: Circle CenterX=-44.8 CenterY=230 CenterZ=0 NormalX=0 NormalY=0 NormalZ=1 AngleXU=0 Radius=0.855
    g48: Circle CenterX=44.8 CenterY=230 CenterZ=0 NormalX=0 NormalY=0 NormalZ=1 AngleXU=0 Radius=0.855
    g49: LineSegment StartX=-34.8 StartY=89.607 StartZ=0 EndX=34.8 EndY=89.607 EndZ=0
    g50: LineSegment StartX=34.8 StartY=89.607 StartZ=0 EndX=34.8 EndY=98.0817 EndZ=0
    g51: LineSegment StartX=34.8 StartY=98.0817 StartZ=0 EndX=-34.8 EndY=98.0817 EndZ=0
    g52: LineSegment StartX=-34.8 StartY=98.0817 StartZ=0 EndX=-34.8 EndY=89.607 EndZ=0
    g53: Circle CenterX=-44.8 CenterY=94 CenterZ=0 NormalX=0 NormalY=0 NormalZ=1 AngleXU=0 Radius=0.855
    g54: Circle CenterX=44.8 CenterY=94 CenterZ=0 NormalX=0 NormalY=0 NormalZ=1 AngleXU=0 Radius=0.85
  constraints (151):
    c: Coincident(g0,g1)
    c: Coincident(g1,g2)
    c: Coincident(g2,g3)
    c: Coincident(g3,g0)
    c: Horizontal(g2)
    c: Vertical(g1)
    c: Vertical(g3)
    c: DistanceY(g0,g2) = 228.6
    c: DistanceX(g0,g0) = 101.6
    c: DistanceX(g0,g-1) = 50.8
    c: Coincident(g4,g5)
    c: Vertical(g4)
    c: Horizontal(g5)
    c: DistanceX(g4,g0) = 4
    c: Horizontal(g0)
    c: Coincident(g6,g7)
    c: Coincident(g7,g8)
    c: Coincident(g8,g9)
    c: Coincident(g9,g6)
    c: Horizontal(g6)
    c: Horizontal(g8)
    c: Vertical(g7)
    c: Vertical(g9)
    c: Coincident(g10,g11)
    c: Coincident(g11,g12)
    c: Coincident(g12,g13)
    c: Coincident(g13,g10)
    c: Horizontal(g10)
    c: Horizontal(g12)
    c: Vertical(g11)
    c: Vertical(g13)
    c: Coincident(g14,g15)
    c: Coincident(g15,g16)
    c: Coincident(g16,g17)
    c: Coincident(g17,g14)
    c: Horizontal(g14)
    c: Horizontal(g16)
    c: Vertical(g15)
    c: Vertical(g17)
    c: Coincident(g18,g19)
    c: Coincident(g19,g20)
    c: Coincident(g20,g21)
    c: Coincident(g21,g18)
    c: Horizontal(g18)
    c: Horizontal(g20)
    c: Vertical(g19)
    c: DistanceY(g20,g16) = 10
    c: Vertical(g12,g18)
    c: DistanceY(g6,g18) = 20
    c: Coincident(g22,g23)
    c: Coincident(g23,g24)
    c: Coincident(g24,g25)
    c: Coincident(g25,g22)
    c: Vertical(g22)
    c: Vertical(g24)
    c: Horizontal(g23)
    c: Horizontal(g25)
    c: Coincident(g26,g27)
    c: Coincident(g27,g28)
    c: Coincident(g28,g29)
    c: Coincident(g29,g26)
    c: Vertical(g26)
    c: Vertical(g28)
    c: Horizontal(g27)
    c: Horizontal(g29)
    c: DistanceY(g26,g22) = 15
    c: Vertical(g22,g26)
    c: Vertical(g10,g24)
    c: Vertical(g24,g28)
    c: Coincident(g30,g5)
    c: Vertical(g30)
    c: DistanceY(g1,g30) = 4
    c: Horizontal(g4,g30)
    c: Coincident(g31,g4)
    c: Coincident(g31,g30)
    c: DistanceX(g4,g5) = 109.6
    c: DistanceY(g-1,g5) = 20
    c: Coincident(g32,g33)
    c: Coincident(g33,g34)
    c: Coincident(g34,g35)
    c: Coincident(g35,g32)
    c: Vertical(g32)
    c: Vertical(g34)
    c: Horizontal(g33)
    c: Horizontal(g35)
    c: Coincident(g32,g4)
    c: Horizontal(g33,g-1)
    c: Vertical(g34,g5)
    c: Vertical(g21)
    c: Coincident(g36,g4)
    c: Vertical(g36)
    c: Coincident(g37,g36)
    c: Horizontal(g37)
    c: Coincident(g38,g37)
    c: Coincident(g38,g30)
    c: Vertical(g38)
    c: DistanceY(g-1,g26) = 9
    c: DistanceX(g32,g26) = 20
    c: DistanceX(g27,g33) = 20
    c: Vertical(g10,g22)
    c: Vertical(g11,g7)
    c: Vertical(g6,g18)
    c: Vertical(g19,g15)
    c: Vertical(g12,g8)
    c: Vertical(g20,g16)
    c: DistanceY(g12,g8) = 15
    c: DistanceY(g33,g37) = 259
    c: Diameter(g39) = 1.71
    c: Diameter(g40) = 1.71
    c: Horizontal(g40,g39)
    c: DistanceX(g4,g39) = 10
    c: DistanceX(g40,g5) = 10
    c: Diameter(g41) = 1.71
    c: Diameter(g42) = 1.71
    c: Horizontal(g42,g41)
    c: Diameter(g43) = 1.71
    c: Diameter(g44) = 1.71
    c: Horizontal(g44,g43)
    c: Vertical(g43,g39)
    c: Vertical(g44,g42)
    c: Diameter(g45) = 1.71
    c: Diameter(g46) = 1.71
    c: Horizontal(g46,g45)
    c: DistanceY(g-1,g39) = 30
    c: DistanceY(g-1,g41) = 112
    c: Vertical(g45,g41)
    c: DistanceY(g-1,g45) = 135
    c: DistanceY(g-1,g43) = 157
    c: Vertical(g42,g46)
    c: Diameter(g48) = 1.71
    c: Diameter(g47) = 1.71
    c: Vertical(g48,g44)
    c: Vertical(g47,g43)
    c: DistanceY(g-1,g47) = 230
    c: Horizontal(g48,g47)
    c: Coincident(g49,g50)
    c: Coincident(g50,g51)
    c: Coincident(g51,g52)
    c: Coincident(g52,g49)
    c: Horizontal(g49)
    c: Horizontal(g51)
    c: Vertical(g50)
    c: Vertical(g52)
    c: Vertical(g49,g22)
    c: Vertical(g49,g24)
    c: Diameter(g53) = 1.71
    c: Vertical(g41,g53)
    c: Diameter(g54) = 1.7
    c: Horizontal(g53,g54)
    c: Vertical(g54,g42)
    c: DistanceY(g-1,g53) = 94
FEATURE [PartDesign::Pad] Pad004  label="Frontplate Pad"
  Direction = (0,-1,2e-16)
  Length = 3
  Length2 = 10
  Placement = pos=(0,0,0) rot=(1,0,0;1.5708rad)
  Profile = -> Sketch005
  ReferenceAxis = -> Sketch005 [N_Axis]
  Reversed = true
  Suppressed = false
  Type = 0
  expr: Length = <<Monitor Chassis Parameters>>.GSBackPlateThickness
FEATURE [Sketcher::SketchObject] Sketch007  label="Frontplate Foot Sketch"
  ArcFitTolerance = 1e-06
  AttachmentSupport = -> [XZ_Plane002]
  FullyConstrained = true
  MakeInternals = false
  MapMode = 5
  Placement = pos=(0,0,0) rot=(1,0,0;1.5708rad)
  expr: Constraints[11] = <<Monitor Chassis Parameters>>.GSTowerFeetThickness
  expr: Constraints[21] = <<Monitor Chassis Parameters>>.GSTowerFeetThickness
  expr: Constraints[22] = <<Monitor Chassis Parameters>>.GSBackPlateFootWidth
  expr: Constraints[23] = 0.5 * <<Monitor Chassis Parameters>>.GSBackPlateWidth
  expr: Constraints[8] = <<Monitor Chassis Parameters>>.GSBackPlateFootWidth
  expr: Constraints[9] = 0.5 * <<Monitor Chassis Parameters>>.GSBackPlateWidth
  sketch-geometry (8):
    g0: LineSegment StartX=-54.8 StartY=-5 StartZ=0 EndX=-19.8 EndY=-5 EndZ=0
    g1: LineSegment StartX=-19.8 StartY=-5 StartZ=0 EndX=-19.8 EndY=0 EndZ=0
    g2: LineSegment StartX=-19.8 StartY=0 StartZ=0 EndX=-54.8 EndY=0 EndZ=0
    g3: LineSegment StartX=-54.8 StartY=0 StartZ=0 EndX=-54.8 EndY=-5 EndZ=0
    g4: LineSegment StartX=54.8 StartY=-5 StartZ=0 EndX=54.8 EndY=0 EndZ=0
    g5: LineSegment StartX=54.8 StartY=0 StartZ=0 EndX=19.8 EndY=0 EndZ=0
    g6: LineSegment StartX=19.8 StartY=0 StartZ=0 EndX=19.8 EndY=-5 EndZ=0
    g7: LineSegment StartX=19.8 StartY=-5 StartZ=0 EndX=54.8 EndY=-5 EndZ=0
  constraints (24):
    c: Coincident(g0,g1)
    c: Coincident(g1,g2)
    c: Coincident(g2,g3)
    c: Coincident(g3,g0)
    c: Horizontal(g0)
    c: Horizontal(g2)
    c: Vertical(g1)
    c: Vertical(g3)
    c: DistanceX(g2,g1) = 35
    c: DistanceX(g2,g-1) = 54.8
    c: Horizontal(g2,g-1)
    c: DistanceY(g0,g2) = 5
    c: Coincident(g4,g5)
    c: Coincident(g5,g6)
    c: Coincident(g6,g7)
    c: Coincident(g7,g4)
    c: Vertical(g4)
    c: Vertical(g6)
    c: Horizontal(g5)
    c: Horizontal(g7)
    c: Horizontal(g5,g-1)
    c: DistanceY(g4,g4) = 5
    c: DistanceX(g6,g4) = 35
    c: DistanceX(g-1,g4) = 54.8
FEATURE [PartDesign::Pad] Pad006  label="Frontplate Foot Pad"
  BaseFeature = -> Pad004
  Direction = (0,-1,2e-16)
  Length = 65
  Length2 = 3
  Placement = pos=(0,0,0) rot=(1,0,0;1.5708rad)
  Profile = -> Sketch007
  ReferenceAxis = -> Sketch007 [N_Axis]
  Suppressed = false
  Type = 4
  expr: Length = <<Monitor Chassis Parameters>>.GSBackPlateFootLengthForward
  expr: Length2 = <<Monitor Chassis Parameters>>.GSBackPlateThickness
FEATURE [Sketcher::SketchObject] Sketch008  label="Frontplate Foot Screw Holes Sketch"
  ArcFitTolerance = 1e-06
  AttachmentSupport = -> [XY_Plane002]
  FullyConstrained = true
  MakeInternals = false
  MapMode = 5
  expr: Constraints[0] = <<Monitor Chassis Parameters>>.GSBackPlateFootScrewHoleForwardOffset
  expr: Constraints[1] = 0.5 * <<Monitor Chassis Parameters>>.GSBackPlateWidth - 0.5 * <<Monitor Chassis Parameters>>.GSBackPlateFootWidth
  expr: Constraints[2] = 0.5 * <<Monitor Chassis Parameters>>.GSBackPlateWidth - 0.5 * <<Monitor Chassis Parameters>>.GSBackPlateFootWidth
  expr: Constraints[3] = <<Monitor Chassis Parameters>>.GSTowerFeetScrewDiameter
  expr: Constraints[4] = <<Monitor Chassis Parameters>>.GSTowerFeetScrewDiameter
  sketch-geometry (2):
    g0: Circle CenterX=-37.3 CenterY=-59 CenterZ=0 NormalX=0 NormalY=0 NormalZ=1 AngleXU=0 Radius=1.7
    g1: Circle CenterX=37.3 CenterY=-59 CenterZ=0 NormalX=0 NormalY=0 NormalZ=1 AngleXU=0 Radius=1.7
  constraints (6):
    c: DistanceY(g0,g-1) = 59
    c: DistanceX(g0,g-1) = 37.3
    c: DistanceX(g-1,g1) = 37.3
    c: Diameter(g0) = 3.4
    c: Diameter(g1) = 3.4
    c: Horizontal(g1,g0)
FEATURE [PartDesign::Hole] Hole001  label="Frontplate Foot Screw Holes"
  BaseFeature = -> Pad006
  CustomThreadClearance = 0
  Depth = 25
  DepthType = 0
  Diameter = 3.4
  DrillForDepth = false
  DrillPoint = 1
  DrillPointAngle = 118
  HoleCutCountersinkAngle = 90
  HoleCutCustomValues = false
  HoleCutDepth = 0
  HoleCutDiameter = 8
  HoleCutType = 2
  ModelThread = false
  Placement = pos=(0,0,0) rot=(1,0,0;1.5708rad)
  Profile = -> Sketch008
  Suppressed = false
  Tapered = false
  TaperedAngle = 90
  ThreadClass = 0
  ThreadDepth = 25
  ThreadDepthType = 0
  ThreadDirection = 0
  ThreadFit = 0
  ThreadSize = 0
  ThreadType = 0
  Threaded = false
  UseCustomThreadClearance = false
  expr: Diameter = <<Monitor Chassis Parameters>>.GSTowerFeetScrewDiameter
  expr: HoleCutDiameter = <<Monitor Chassis Parameters>>.GSM4BoltCountersinkDiameter
FEATURE [Sketcher::SketchObject] Sketch009  label="Frontplate Foot Support Corner Sketch"
  ArcFitTolerance = 1e-06
  AttachmentSupport = -> [DatumPlane001]
  FullyConstrained = true
  MakeInternals = false
  MapMode = 5
  Placement = pos=(54.8,0,0) rot=(0.57735,0.57735,0.57735;2.0944rad)
  expr: Constraints[1] = <<Monitor Chassis Parameters>>.GSBackPlateThickness
  expr: Constraints[24] = 0.8 * <<Monitor Chassis Parameters>>.GSTowerFloorDepth
  expr: Constraints[25] = 0.6 * <<Monitor Chassis Parameters>>.GSTowerFloorDepth
  expr: Constraints[26] = <<Monitor Chassis Parameters>>.GSSideCornerCutoutInset
  expr: Constraints[27] = <<Monitor Chassis Parameters>>.GSSideCornerCutoutInset
  expr: Constraints[28] = 2 * <<Monitor Chassis Parameters>>.GSSideCornerCutoutInset
  expr: Constraints[29] = 3 * <<Monitor Chassis Parameters>>.GSSideCornerCutoutInset
  expr: Constraints[39] = 0.8 * <<Monitor Chassis Parameters>>.GSTowerFloorDepth
  expr: Constraints[3] = <<Monitor Chassis Parameters>>.GSTowerFeetThickness
  expr: Constraints[41] = <<Monitor Chassis Parameters>>.GSSideCornerCutoutInset
  expr: Constraints[42] = -2 * <<Monitor Chassis Parameters>>.GSSideCornerCutoutInset
  expr: Constraints[43] = 3 * <<Monitor Chassis Parameters>>.GSSideCornerCutoutInset
  expr: Constraints[54] = 0.8 * <<Monitor Chassis Parameters>>.GSTowerFloorDepth
  expr: Constraints[55] = 0.6 * <<Monitor Chassis Parameters>>.GSTowerFloorDepth
  expr: Constraints[56] = <<Monitor Chassis Parameters>>.GSSideCornerCutoutInset
  expr: Constraints[57] = <<Monitor Chassis Parameters>>.GSSideCornerCutoutInset
  expr: Constraints[58] = 2 * <<Monitor Chassis Parameters>>.GSSideCornerCutoutInset
  expr: Constraints[59] = 3 * <<Monitor Chassis Parameters>>.GSSideCornerCutoutInset
  expr: Constraints[62] = <<Monitor Chassis Parameters>>.GSTowerThirdFloorHeight
  expr: Constraints[63] = <<Monitor Chassis Parameters>>.GSTowerSecondFloorHeight
  expr: Constraints[64] = 0.6 * <<Monitor Chassis Parameters>>.GSTowerFloorDepth
  expr: Constraints[65] = <<Monitor Chassis Parameters>>.GSTowerFourthFloorHeight + <<Monitor Chassis Parameters>>.GSTowerFloorThickness
  expr: Constraints[6] = 0.8 * <<Monitor Chassis Parameters>>.GSTowerFloorDepth
  expr: Constraints[70] = 2 * <<Monitor Chassis Parameters>>.GSSideCornerCutoutInset
  expr: Constraints[71] = 3 * <<Monitor Chassis Parameters>>.GSSideCornerCutoutInset
  expr: Constraints[73] = <<Monitor Chassis Parameters>>.GSSideCornerCutoutInset
  expr: Constraints[7] = 0.6 * <<Monitor Chassis Parameters>>.GSTowerFloorDepth
  sketch-geometry (24):
    g0: LineSegment StartX=-41 StartY=-5 StartZ=0 EndX=3 EndY=-5 EndZ=0
    g1: LineSegment StartX=3 StartY=28 StartZ=0 EndX=3 EndY=-5 EndZ=0
    g2: LineSegment StartX=-41 StartY=-5 StartZ=0 EndX=3 EndY=28 EndZ=0
    g3: LineSegment StartX=-23 StartY=181 StartZ=0 EndX=-3 EndY=196 EndZ=0
    g4: LineSegment StartX=-3 StartY=196 StartZ=0 EndX=-3 EndY=181 EndZ=0
    g5: LineSegment StartX=-23 StartY=181 StartZ=0 EndX=-3 EndY=181 EndZ=0
    g6: LineSegment StartX=3 StartY=208 StartZ=0 EndX=3 EndY=175 EndZ=0
    g7: LineSegment StartX=3 StartY=175 StartZ=0 EndX=-41 EndY=175 EndZ=0
    g8: LineSegment StartX=-41 StartY=175 StartZ=0 EndX=3 EndY=208 EndZ=0
    g9: LineSegment StartX=-23 StartY=1 StartZ=0 EndX=-3 EndY=16 EndZ=0
    g10: LineSegment StartX=-3 StartY=16 StartZ=0 EndX=-3 EndY=1 EndZ=0
    g11: LineSegment StartX=-23 StartY=1 StartZ=0 EndX=-3 EndY=1 EndZ=0
    g12: LineSegment StartX=-23 StartY=253 StartZ=0 EndX=-3 EndY=238 EndZ=0
    g13: LineSegment StartX=-3 StartY=238 StartZ=0 EndX=-3 EndY=253 EndZ=0
    g14: LineSegment StartX=-23 StartY=253 StartZ=0 EndX=-3 EndY=253 EndZ=0
    g15: LineSegment StartX=3 StartY=226 StartZ=0 EndX=3 EndY=259 EndZ=0
    g16: LineSegment StartX=3 StartY=259 StartZ=0 EndX=-41 EndY=259 EndZ=0
    g17: LineSegment StartX=-41 StartY=259 StartZ=0 EndX=3 EndY=226 EndZ=0
    g18: LineSegment StartX=-23 StartY=91 StartZ=0 EndX=-3 EndY=106 EndZ=0
    g19: LineSegment StartX=-3 StartY=106 StartZ=0 EndX=-3 EndY=91 EndZ=0
    g20: LineSegment StartX=-23 StartY=91 StartZ=0 EndX=-3 EndY=91 EndZ=0
    g21: LineSegment StartX=3 StartY=118 StartZ=0 EndX=3 EndY=85 EndZ=0
    g22: LineSegment StartX=3 StartY=85 StartZ=0 EndX=-41 EndY=85 EndZ=0
    g23: LineSegment StartX=-41 StartY=85 StartZ=0 EndX=3 EndY=118 EndZ=0
  constraints (74):
    c: Horizontal(g0)
    c: DistanceX(g-1,g0) = 3
    c: Vertical(g1)
    c: DistanceY(g0,g-1) = 5
    c: Coincident(g2,g0)
    c: Coincident(g2,g1)
    c: DistanceX(g0,g0) = 44
    c: DistanceY(g0,g1) = 33
    c: Coincident(g4,g3)
    c: Vertical(g4)
    c: Coincident(g5,g3)
    c: Coincident(g5,g4)
    c: Horizontal(g5)
    c: Vertical(g6)
    c: Coincident(g7,g6)
    c: Horizontal(g7)
    c: Coincident(g8,g7)
    c: Coincident(g8,g6)
    c: Coincident(g10,g9)
    c: Vertical(g10)
    c: Coincident(g11,g9)
    c: Coincident(g11,g10)
    c: Horizontal(g11)
    c: Vertical(g6,g1)
    c: DistanceX(g7,g6) = 44
    c: DistanceY(g6,g6) = 33
    c: DistanceY(g6,g4) = 6
    c: DistanceX(g4,g6) = 6
    c: DistanceY(g3,g6) = 12
    c: DistanceX(g7,g3) = 18
    c: Coincident(g13,g12)
    c: Vertical(g13)
    c: Coincident(g14,g12)
    c: Coincident(g14,g13)
    c: Horizontal(g14)
    c: Vertical(g15)
    c: Horizontal(g16)
    c: Coincident(g17,g16)
    c: Coincident(g17,g15)
    c: DistanceX(g16,g15) = 44
    c: DistanceY(g15,g13) = -6
    c: DistanceX(g13,g15) = 6
    c: DistanceY(g12,g15) = -12
    c: DistanceX(g16,g12) = 18
    c: Coincident(g19,g18)
    c: Vertical(g19)
    c: Coincident(g20,g18)
    c: Coincident(g20,g19)
    c: Horizontal(g20)
    c: Vertical(g21)
    c: Coincident(g22,g21)
    c: Horizontal(g22)
    c: Coincident(g23,g22)
    c: Coincident(g23,g21)
    c: DistanceX(g22,g21) = 44
    c: DistanceY(g21,g21) = 33
    c: DistanceY(g21,g19) = 6
    c: DistanceX(g19,g21) = 6
    c: DistanceY(g18,g21) = 12
    c: DistanceX(g22,g18) = 18
    c: Vertical(g21,g6)
    c: Vertical(g6,g15)
    c: DistanceY(g-1,g6) = 175
    c: DistanceY(g-1,g21) = 85
    c: DistanceY(g15,g15) = 33
    c: DistanceY(g-1,g15) = 259
    c: Horizontal(g16,g15)
    c: Vertical(g16,g15)
    c: Vertical(g1,g0)
    c: Horizontal(g1,g0)
    c: DistanceY(g9,g1) = 12
    c: DistanceX(g0,g9) = 18
    c: Vertical(g19,g9)
    c: DistanceY(g0,g10) = 6
FEATURE [PartDesign::Pad] Pad007  label="Frontplate Floor Support Corner Pad"
  BaseFeature = -> Hole001
  Direction = (1,0,0)
  Length = 2.5
  Length2 = 10
  Placement = pos=(0,0,0) rot=(1,0,0;1.5708rad)
  Profile = -> Sketch009
  ReferenceAxis = -> Sketch009 [N_Axis]
  Suppressed = false
  Type = 0
  expr: Length = <<Monitor Chassis Parameters>>.GSSideCornerThickness
FEATURE [PartDesign::Mirrored] Mirrored001  label="Frontplate Floor Support Corner Mirrored"
  BaseFeature = -> Pad007
  MirrorPlane = -> YZ_Plane002
  Originals = -> [Pad007]
  Placement = pos=(0,0,0) rot=(1,0,0;1.5708rad)
  Suppressed = false
  TransformMode = 0
FEATURE [Sketcher::SketchObject] Sketch010  label="Frontplate Floors Sketch"
  ArcFitTolerance = 1e-06
  AttachmentSupport = -> [DatumPlane001]
  FullyConstrained = true
  MakeInternals = false
  MapMode = 5
  Placement = pos=(54.8,0,0) rot=(0.57735,0.57735,0.57735;2.0944rad)
  expr: Constraints[10] = <<Monitor Chassis Parameters>>.GSTowerSecondFloorDepth
  expr: Constraints[21] = <<Monitor Chassis Parameters>>.GSTowerFourthFloorDepth
  expr: Constraints[32] = <<Monitor Chassis Parameters>>.GSTowerThirdFloorDepth
  expr: Constraints[43] = <<Monitor Chassis Parameters>>.GSTowerFirstFloorDepth
  expr: Constraints[44] = <<Monitor Chassis Parameters>>.GSTowerFirstFloorHeight
  expr: Constraints[45] = <<Monitor Chassis Parameters>>.GSTowerSecondFloorHeight
  expr: Constraints[46] = <<Monitor Chassis Parameters>>.GSTowerFourthFloorHeight
  expr: Constraints[47] = <<Monitor Chassis Parameters>>.GSTowerThirdFloorHeight
  expr: Constraints[9] = <<Monitor Chassis Parameters>>.GSTowerFloorThickness
  sketch-geometry (16):
    g0: LineSegment StartX=-55 StartY=85 StartZ=0 EndX=0 EndY=85 EndZ=0
    g1: LineSegment StartX=0 StartY=85 StartZ=0 EndX=0 EndY=89 EndZ=0
    g2: LineSegment StartX=0 StartY=89 StartZ=0 EndX=-55 EndY=89 EndZ=0
    g3: LineSegment StartX=-55 StartY=89 StartZ=0 EndX=-55 EndY=85 EndZ=0
    g4: LineSegment StartX=-55 StartY=255 StartZ=0 EndX=0 EndY=255 EndZ=0
    g5: LineSegment StartX=0 StartY=255 StartZ=0 EndX=0 EndY=259 EndZ=0
    g6: LineSegment StartX=0 StartY=259 StartZ=0 EndX=-55 EndY=259 EndZ=0
    g7: LineSegment StartX=-55 StartY=259 StartZ=0 EndX=-55 EndY=255 EndZ=0
    g8: LineSegment StartX=-55 StartY=175 StartZ=0 EndX=0 EndY=175 EndZ=0
    g9: LineSegment StartX=0 StartY=175 StartZ=0 EndX=0 EndY=179 EndZ=0
    g10: LineSegment StartX=0 StartY=179 StartZ=0 EndX=-55 EndY=179 EndZ=0
    g11: LineSegment StartX=-55 StartY=179 StartZ=0 EndX=-55 EndY=175 EndZ=0
    g12: LineSegment StartX=-50 StartY=5 StartZ=0 EndX=0 EndY=5 EndZ=0
    g13: LineSegment StartX=0 StartY=5 StartZ=0 EndX=0 EndY=9 EndZ=0
    g14: LineSegment StartX=0 StartY=9 StartZ=0 EndX=-50 EndY=9 EndZ=0
    g15: LineSegment StartX=-50 StartY=9 StartZ=0 EndX=-50 EndY=5 EndZ=0
  constraints (48):
    c: Coincident(g0,g1)
    c: Coincident(g1,g2)
    c: Coincident(g2,g3)
    c: Coincident(g3,g0)
    c: Horizontal(g0)
    c: Horizontal(g2)
    c: Vertical(g1)
    c: Vertical(g3)
    c: Vertical(g0,g-1)
    c: DistanceY(g0,g2) = 4
    c: DistanceX(g2,g1) = 55
    c: Coincident(g4,g5)
    c: Coincident(g5,g6)
    c: Coincident(g6,g7)
    c: Coincident(g7,g4)
    c: Horizontal(g4)
    c: Horizontal(g6)
    c: Vertical(g5)
    c: Vertical(g7)
    c: Vertical(g4,g-1)
    c: DistanceY(g4,g6) = 4
    c: DistanceX(g6,g5) = 55
    c: Coincident(g8,g9)
    c: Coincident(g9,g10)
    c: Coincident(g10,g11)
    c: Coincident(g11,g8)
    c: Horizontal(g8)
    c: Horizontal(g10)
    c: Vertical(g9)
    c: Vertical(g11)
    c: Vertical(g8,g-1)
    c: DistanceY(g8,g10) = 4
    c: DistanceX(g10,g9) = 55
    c: Coincident(g12,g13)
    c: Coincident(g13,g14)
    c: Coincident(g14,g15)
    c: Coincident(g15,g12)
    c: Horizontal(g12)
    c: Horizontal(g14)
    c: Vertical(g13)
    c: Vertical(g15)
    c: Vertical(g12,g-1)
    c: DistanceY(g12,g14) = 4
    c: DistanceX(g14,g13) = 50
    c: DistanceY(g-1,g12) = 5
    c: DistanceY(g-1,g0) = 85
    c: DistanceY(g-1,g4) = 255
    c: DistanceY(g-1,g8) = 175
FEATURE [PartDesign::Pad] Pad008  label="Tower Floors Pad"
  BaseFeature = -> Mirrored001
  Direction = (1,0,0)
  Length = 109.6
  Length2 = 10
  Placement = pos=(0,0,0) rot=(1,0,0;1.5708rad)
  Profile = -> Sketch010
  ReferenceAxis = -> Sketch010 [N_Axis]
  Reversed = true
  Suppressed = false
  Type = 0
  expr: Length = <<Monitor Chassis Parameters>>.GSBackPlateWidth
FEATURE [PartDesign::Plane] DatumPlane002  label="First Floor DatumPlane"
  AttachmentOffset = pos=(0,0,9) rot=(0,0,1;0rad)
  AttachmentSupport = -> [XY_Plane002]
  Length = 134.912
  MapMode = 5
  Placement = pos=(0,0,9) rot=(0,0,1;0rad)
  ResizeMode = 0
  Width = 110.312
  expr: .AttachmentOffset.Base.z = <<Monitor Chassis Parameters>>.GSTowerFirstFloorHeight + <<Monitor Chassis Parameters>>.GSTowerFloorThickness
FEATURE [PartDesign::Plane] DatumPlane003  label="Second Floor DatumPlane"
  AttachmentOffset = pos=(0,0,89) rot=(0,0,1;0rad)
  AttachmentSupport = -> [XY_Plane002]
  Length = 134.912
  MapMode = 5
  Placement = pos=(0,0,89) rot=(0,0,1;0rad)
  ResizeMode = 0
  Width = 110.312
  expr: .AttachmentOffset.Base.z = <<Monitor Chassis Parameters>>.GSTowerSecondFloorHeight + <<Monitor Chassis Parameters>>.GSTowerFloorThickness
FEATURE [PartDesign::Plane] DatumPlane004  label="Third Floor DatumPlane"
  AttachmentOffset = pos=(0,0,179) rot=(0,0,1;0rad)
  AttachmentSupport = -> [XY_Plane002]
  Length = 134.912
  MapMode = 5
  Placement = pos=(0,0,179) rot=(0,0,1;0rad)
  ResizeMode = 0
  Width = 110.312
  expr: .AttachmentOffset.Base.z = <<Monitor Chassis Parameters>>.GSTowerThirdFloorHeight + <<Monitor Chassis Parameters>>.GSTowerFloorThickness
FEATURE [Sketcher::SketchObject] Sketch011  label="Third Floor Holes Sketch"
  ArcFitTolerance = 1e-06
  AttachmentSupport = -> [DatumPlane004]
  FullyConstrained = true
  MakeInternals = false
  MapMode = 5
  Placement = pos=(0,0,179) rot=(0,0,1;0rad)
  expr: Constraints[1] = 2 + 0.5 * <<Monitor Chassis Parameters>>.GSTowerThirdFloorDepth
  expr: Constraints[2] = <<Monitor Chassis Parameters>>.GSMonitorFloorCameraMountHoleDiameter
  sketch-geometry (1):
    g0: Circle CenterX=0 CenterY=-29.5 CenterZ=0 NormalX=0 NormalY=0 NormalZ=1 AngleXU=0 Radius=2.75
  constraints (3):
    c: PointOnObject(g0,g-2)
    c: DistanceY(g0,g-1) = 29.5
    c: Diameter(g0) = 5.5
FEATURE [PartDesign::Pocket] Pocket  label="Third Floor Holes Pocket"
  BaseFeature = -> Pad008
  Direction = (0,0,-1)
  Length = 5
  Length2 = 5
  Placement = pos=(0,0,0) rot=(1,0,0;1.5708rad)
  Profile = -> Sketch011
  ReferenceAxis = -> Sketch011 [N_Axis]
  Suppressed = false
  Type = 0
FEATURE [Sketcher::SketchObject] Sketch012  label="Second Floor Holes Sketch"
  ArcFitTolerance = 1e-06
  AttachmentSupport = -> [DatumPlane003]
  FullyConstrained = true
  MakeInternals = false
  MapMode = 2
  Placement = pos=(0,0,89) rot=(0,0,1;0rad)
  expr: Constraints[0] = <<Monitor Chassis Parameters>>.GSMonitorFloorCameraMountHoleDiameter
  expr: Constraints[2] = 12 + 0.4 * <<Monitor Chassis Parameters>>.GSTowerSecondFloorDepth
  sketch-geometry (1):
    g0: Circle CenterX=0 CenterY=-34 CenterZ=0 NormalX=0 NormalY=0 NormalZ=1 AngleXU=0 Radius=2.75
  constraints (3):
    c: Diameter(g0) = 5.5
    c: Vertical(g-1,g0)
    c: DistanceY(g0,g-1) = 34
FEATURE [PartDesign::Pocket] Pocket001  label="Second Floor Holes Pocket"
  BaseFeature = -> Pocket
  Direction = (0,0,-1)
  Length = 5
  Length2 = 5
  Placement = pos=(0,0,0) rot=(1,0,0;1.5708rad)
  Profile = -> Sketch012
  ReferenceAxis = -> Sketch012 [N_Axis]
  Suppressed = false
  Type = 0
FEATURE [Sketcher::SketchObject] Sketch013  label="First Floor Holes Sketch"
  ArcFitTolerance = 1e-06
  AttachmentSupport = -> [DatumPlane002]
  FullyConstrained = true
  MakeInternals = false
  MapMode = 5
  Placement = pos=(0,0,9) rot=(0,0,1;0rad)
  expr: Constraints[0] = <<Monitor Chassis Parameters>>.GSMonitorFloorCameraMountHoleDiameter
  expr: Constraints[2] = 0.5 * <<Monitor Chassis Parameters>>.GSTowerFirstFloorDepth
  sketch-geometry (1):
    g0: Circle CenterX=0 CenterY=-25 CenterZ=0 NormalX=0 NormalY=0 NormalZ=1 AngleXU=0 Radius=2.75
  constraints (3):
    c: Diameter(g0) = 5.5
    c: Vertical(g0,g-1)
    c: DistanceY(g0,g-1) = 25
FEATURE [PartDesign::Pocket] Pocket002  label="First Floor Holes Pocket"
  BaseFeature = -> Pocket001
  Direction = (0,0,-1)
  Length = 5
  Length2 = 5
  Placement = pos=(0,0,0) rot=(1,0,0;1.5708rad)
  Profile = -> Sketch013
  ReferenceAxis = -> Sketch013 [N_Axis]
  Suppressed = false
  Type = 0
FEATURE [Sketcher::SketchObject] Sketch014  label="Shank Shield Riser Sketch"
  ArcFitTolerance = 1e-06
  AttachmentSupport = -> [XZ_Plane002]
  FullyConstrained = true
  MakeInternals = false
  MapMode = 5
  Placement = pos=(0,0,0) rot=(1,0,0;1.5708rad)
  expr: Constraints[0] = 3 * <<Monitor Chassis Parameters>>.GSM4TappingScrewHoleDiameter
  expr: Constraints[1] = <<Monitor Chassis Parameters>>.GSTowerFourthFloorHeight - 1.5 * <<Monitor Chassis Parameters>>.GSM4TappingScrewHoleDiameter
  expr: Constraints[2] = 0.5 * <<Monitor Chassis Parameters>>.GSBackPlateWidth - 1.5 * <<Monitor Chassis Parameters>>.GSM4TappingScrewHoleDiameter
  expr: Constraints[3] = 3 * <<Monitor Chassis Parameters>>.GSM4TappingScrewHoleDiameter
  expr: Constraints[5] = <<Monitor Chassis Parameters>>.GSBackPlateWidth - 3 * <<Monitor Chassis Parameters>>.GSM4TappingScrewHoleDiameter
  sketch-geometry (2):
    g0: Circle CenterX=-49.7 CenterY=249.9 CenterZ=0 NormalX=0 NormalY=0 NormalZ=1 AngleXU=0 Radius=5.1
    g1: Circle CenterX=49.7 CenterY=249.9 CenterZ=0 NormalX=0 NormalY=0 NormalZ=1 AngleXU=0 Radius=5.1
  constraints (6):
    c: Diameter(g0) = 10.2
    c: DistanceY(g-1,g0) = 249.9
    c: DistanceX(g0,g-1) = 49.7
    c: Diameter(g1) = 10.2
    c: Horizontal(g0,g1)
    c: DistanceX(g0,g1) = 99.4
FEATURE [PartDesign::Pad] Pad009  label="Shank Shield Riser Pad"
  BaseFeature = -> Pocket002
  Direction = (0,-1,2e-16)
  Length = 89.65
  Length2 = 10
  Placement = pos=(0,0,0) rot=(1,0,0;1.5708rad)
  Profile = -> Sketch014
  ReferenceAxis = -> Sketch014 [N_Axis]
  Suppressed = false
  Type = 0
  expr: Length = 1 + <<Monitor Chassis Parameters>>.GSBasePowerBoxTowerBackOffsetFromFront - <<Monitor Chassis Parameters>>.GSShankShieldThickness - <<Monitor Chassis Parameters>>.GSBackPlateThickness - 3 * <<Monitor Chassis Parameters>>.GSBasePowerBoxSideThickness
FEATURE [PartDesign::Plane] DatumPlane005  label="Shank Shield Riser Front DatumPlane005"
  AttachmentSupport = -> [Pad009]
  Length = 150.681
  MapMode = 5
  Placement = pos=(0,-89.65,0) rot=(1,0,0;1.5708rad)
  ResizeMode = 0
  Width = 320.081
FEATURE [Sketcher::SketchObject] Sketch015  label="Shank Shield Riser Screw Holes Sketch"
  ArcFitTolerance = 1e-06
  AttachmentSupport = -> [DatumPlane005]
  FullyConstrained = true
  MakeInternals = false
  MapMode = 5
  Placement = pos=(0,-89.65,0) rot=(1,0,0;1.5708rad)
  expr: Constraints[0] = 0.5 * <<Monitor Chassis Parameters>>.GSBackPlateWidth - 1.5 * <<Monitor Chassis Parameters>>.GSM4TappingScrewHoleDiameter
  expr: Constraints[1] = <<Monitor Chassis Parameters>>.GSM4TappingScrewHoleDiameter
  expr: Constraints[3] = <<Monitor Chassis Parameters>>.GSTowerFourthFloorHeight - 1.5 * <<Monitor Chassis Parameters>>.GSM4TappingScrewHoleDiameter
  expr: Constraints[4] = 0.5 * <<Monitor Chassis Parameters>>.GSBackPlateWidth - 1.5 * <<Monitor Chassis Parameters>>.GSM4TappingScrewHoleDiameter
  expr: Constraints[5] = <<Monitor Chassis Parameters>>.GSM4TappingScrewHoleDiameter
  sketch-geometry (2):
    g0: Circle CenterX=-49.7 CenterY=249.9 CenterZ=0 NormalX=0 NormalY=0 NormalZ=1 AngleXU=0 Radius=1.7
    g1: Circle CenterX=49.7 CenterY=249.9 CenterZ=0 NormalX=0 NormalY=0 NormalZ=1 AngleXU=0 Radius=1.7
  constraints (6):
    c: DistanceX(g0,g-1) = 49.7
    c: Diameter(g0) = 3.4
    c: Horizontal(g0,g1)
    c: DistanceY(g-1,g0) = 249.9
    c: DistanceX(g-1,g1) = 49.7
    c: Diameter(g1) = 3.4
FEATURE [PartDesign::Pocket] Pocket003  label="Shank Shield Riser Screw Holes Pocket"
  BaseFeature = -> Pad009
  Direction = (0,1,-2e-16)
  Length = 14
  Length2 = 5
  Placement = pos=(0,0,0) rot=(1,0,0;1.5708rad)
  Profile = -> Sketch015
  ReferenceAxis = -> Sketch015 [N_Axis]
  Suppressed = false
  Type = 0
  expr: Length = 14
FEATURE [PartDesign::Plane] DatumPlane006  label="Fourth Floor DatumPlane"
  AttachmentOffset = pos=(0,0,259) rot=(0,0,1;0rad)
  AttachmentSupport = -> [XY_Plane002]
  Length = 134.912
  MapMode = 5
  Placement = pos=(0,0,259) rot=(0,0,1;0rad)
  ResizeMode = 0
  Width = 110.312
  expr: .AttachmentOffset.Base.z = <<Monitor Chassis Parameters>>.GSTowerFourthFloorHeight + <<Monitor Chassis Parameters>>.GSTowerFloorThickness
FEATURE [Sketcher::SketchObject] Sketch016  label="Fourth Floor Cutout Sketch"
  ArcFitTolerance = 1e-06
  AttachmentSupport = -> [DatumPlane006]
  FullyConstrained = false
  MakeInternals = false
  MapMode = 5
  Placement = pos=(0,0,259) rot=(0,0,1;0rad)
  sketch-geometry (4):
    g0: LineSegment StartX=-44.9421 StartY=-8.20433 StartZ=0 EndX=-44.9421 EndY=-45.1974 EndZ=0
    g1: LineSegment StartX=-44.9421 StartY=-45.1974 StartZ=0 EndX=49.6477 EndY=-45.1974 EndZ=0
    g2: LineSegment StartX=49.6477 StartY=-45.1974 StartZ=0 EndX=49.6477 EndY=-8.20433 EndZ=0
    g3: LineSegment StartX=49.6477 StartY=-8.20433 StartZ=0 EndX=-44.9421 EndY=-8.20433 EndZ=0
  constraints (8):
    c: Coincident(g0,g1)
    c: Coincident(g1,g2)
    c: Coincident(g2,g3)
    c: Coincident(g3,g0)
    c: Vertical(g0)
    c: Vertical(g2)
    c: Horizontal(g1)
    c: Horizontal(g3)
FEATURE [PartDesign::Plane] DatumPlane007  label="Suggested Backplate Split DatumPlane"
  AttachmentOffset = pos=(0,0,102) rot=(0,0,1;0rad)
  AttachmentSupport = -> [XY_Plane001]
  Length = 124.74
  MapMode = 5
  Placement = pos=(0,0,102) rot=(0,0,1;0rad)
  ResizeMode = 0
  Width = 67.4279
  expr: .AttachmentOffset.Base.z = 102
FEATURE [PartDesign::Plane] DatumPlane008  label="Suggested Frontplate Split DatumPlane"
  AttachmentOffset = pos=(0,0,145) rot=(0,0,1;0rad)
  AttachmentSupport = -> [XY_Plane002]
  Length = 134.912
  MapMode = 5
  Placement = pos=(0,0,145) rot=(0,0,1;0rad)
  ResizeMode = 0
  Width = 110.312
FEATURE [PartDesign::Body] Body001  label="Frontplate Body (same as other variant)"
  AllowCompound = false
  Group = -> [Sketch005,Pad004,Sketch007,Pad006,Sketch008,Hole001,DatumPlane001,Sketch009,Pad007,Mirrored001,Sketch010,Pad008,DatumPlane002,DatumPlane003,DatumPlane004,Sketch011,Pocket,Sketch012,Pocket001,Sketch013,Pocket002,Sketch014,Pad009,DatumPlane005,Sketch015,Pocket003,DatumPlane006,Sketch016,DatumPlane008]
  Origin = -> Origin002
  Placement = pos=(0.1,5,0) rot=(0,0,1;3.14159rad)
  Tip = -> Pocket003
FEATURE [Sketcher::SketchObject] Sketch017  label="Tower Layer Join Screw Holes Sketch"
  ArcFitTolerance = 1e-06
  AttachmentSupport = -> [XZ_Plane001]
  FullyConstrained = true
  MakeInternals = false
  MapMode = 5
  Placement = pos=(0,0,0) rot=(1,0,0;1.5708rad)
  expr: Constraints[0] = <<Monitor Chassis Parameters>>.GSTowerLayerJoinScrewDiameter
  expr: Constraints[1] = <<Monitor Chassis Parameters>>.GSM2TappingScrewHoleDiameter
  expr: Constraints[22] = 0.5 * <<Monitor Chassis Parameters>>.GSBackPlateWidth - <<Monitor Chassis Parameters>>.GSTowerLayerJoinScrewInset
  expr: Constraints[23] = 0.5 * <<Monitor Chassis Parameters>>.GSBackPlateWidth - <<Monitor Chassis Parameters>>.GSTowerLayerJoinScrewInset
  expr: Constraints[24] = <<Monitor Chassis Parameters>>.GSTowerLayerJoinScrewHeightFromFoot_1
  expr: Constraints[25] = <<Monitor Chassis Parameters>>.GSTowerLayerJoinScrewHeightFromFoot_2
  expr: Constraints[26] = <<Monitor Chassis Parameters>>.GSTowerLayerJoinScrewHeightFromFoot_3
  expr: Constraints[27] = <<Monitor Chassis Parameters>>.GSTowerLayerJoinScrewHeightFromFoot_4
  expr: Constraints[28] = <<Monitor Chassis Parameters>>.GSTowerLayerJoinScrewHeightFromFoot_5
  expr: Constraints[29] = <<Monitor Chassis Parameters>>.GSM2TappingScrewHoleDiameter
  expr: Constraints[2] = <<Monitor Chassis Parameters>>.GSM2TappingScrewHoleDiameter
  expr: Constraints[30] = <<Monitor Chassis Parameters>>.GSM2TappingScrewHoleDiameter
  expr: Constraints[35] = <<Monitor Chassis Parameters>>.GSTowerLayerJoinScrewHeightFromFoot_6
  expr: Constraints[3] = <<Monitor Chassis Parameters>>.GSM2TappingScrewHoleDiameter
  expr: Constraints[4] = <<Monitor Chassis Parameters>>.GSM2TappingScrewHoleDiameter
  expr: Constraints[5] = <<Monitor Chassis Parameters>>.GSM2TappingScrewHoleDiameter
  expr: Constraints[6] = <<Monitor Chassis Parameters>>.GSM2TappingScrewHoleDiameter
  expr: Constraints[7] = <<Monitor Chassis Parameters>>.GSM2TappingScrewHoleDiameter
  expr: Constraints[8] = <<Monitor Chassis Parameters>>.GSM2TappingScrewHoleDiameter
  expr: Constraints[9] = <<Monitor Chassis Parameters>>.GSM2TappingScrewHoleDiameter
  sketch-geometry (12):
    g0: Circle CenterX=44.8 CenterY=157 CenterZ=0 NormalX=0 NormalY=0 NormalZ=1 AngleXU=0 Radius=0.855
    g1: Circle CenterX=-44.8 CenterY=135 CenterZ=0 NormalX=0 NormalY=0 NormalZ=1 AngleXU=0 Radius=0.855
    g2: Circle CenterX=44.8 CenterY=135 CenterZ=0 NormalX=0 NormalY=0 NormalZ=1 AngleXU=0 Radius=0.855
    g3: Circle CenterX=-44.8 CenterY=112 CenterZ=0 NormalX=0 NormalY=0 NormalZ=1 AngleXU=0 Radius=0.855
    g4: Circle CenterX=-44.8 CenterY=94 CenterZ=0 NormalX=0 NormalY=0 NormalZ=1 AngleXU=0 Radius=0.855
    g5: Circle CenterX=44.8 CenterY=112 CenterZ=0 NormalX=0 NormalY=0 NormalZ=1 AngleXU=0 Radius=0.855
    g6: Circle CenterX=44.8 CenterY=94 CenterZ=0 NormalX=0 NormalY=0 NormalZ=1 AngleXU=0 Radius=0.855
    g7: Circle CenterX=-44.8 CenterY=30 CenterZ=0 NormalX=0 NormalY=0 NormalZ=1 AngleXU=0 Radius=0.855
    g8: Circle CenterX=44.8 CenterY=30 CenterZ=0 NormalX=0 NormalY=0 NormalZ=1 AngleXU=0 Radius=0.855
    g9: Circle CenterX=-44.8 CenterY=157 CenterZ=0 NormalX=0 NormalY=0 NormalZ=1 AngleXU=0 Radius=0.855
    g10: Circle CenterX=-44.8 CenterY=230 CenterZ=0 NormalX=0 NormalY=0 NormalZ=1 AngleXU=0 Radius=0.855
    g11: Circle CenterX=44.8 CenterY=230 CenterZ=0 NormalX=0 NormalY=0 NormalZ=1 AngleXU=0 Radius=0.855
  constraints (36):
    c: Diameter(g0) = 1.71
    c: Diameter(g1) = 1.71
    c: Diameter(g2) = 1.71
    c: Diameter(g3) = 1.71
    c: Diameter(g4) = 1.71
    c: Diameter(g5) = 1.71
    c: Diameter(g6) = 1.71
    c: Diameter(g7) = 1.71
    c: Diameter(g8) = 1.71
    c: Diameter(g9) = 1.71
    c: Vertical(g9,g1)
    c: Vertical(g1,g3)
    c: Vertical(g4,g3)
    c: Vertical(g7,g4)
    c: Vertical(g8,g6)
    c: Vertical(g6,g5)
    c: Vertical(g5,g2)
    c: Vertical(g0,g2)
    c: Horizontal(g2,g1)
    c: Horizontal(g3,g5)
    c: Horizontal(g4,g6)
    c: Horizontal(g7,g8)
    c: DistanceX(g7,g-1) = 44.8
    c: DistanceX(g-1,g8) = 44.8
    c: DistanceY(g-1,g7) = 30
    c: DistanceY(g-1,g4) = 94
    c: DistanceY(g-1,g3) = 112
    c: DistanceY(g-1,g1) = 135
    c: DistanceY(g-1,g9) = 157
    c: Diameter(g11) = 1.71
    c: Diameter(g10) = 1.71
    c: Horizontal(g9,g0)
    c: Vertical(g0,g11)
    c: Horizontal(g10,g11)
    c: Vertical(g10,g9)
    c: DistanceY(g-1,g10) = 230
FEATURE [PartDesign::Hole] Hole002  label="Plate Connection Holes"
  BaseFeature = -> Mirrored
  CustomThreadClearance = 0
  Depth = 25
  DepthType = 0
  Diameter = 1.71
  DrillForDepth = false
  DrillPoint = 1
  DrillPointAngle = 118
  HoleCutCountersinkAngle = 90
  HoleCutCustomValues = false
  HoleCutDepth = 0
  HoleCutDiameter = 3.5
  HoleCutType = 2
  ModelThread = false
  Placement = pos=(0,0,0) rot=(1,0,0;1.5708rad)
  Profile = -> Sketch017
  Suppressed = false
  Tapered = false
  TaperedAngle = 90
  ThreadClass = 0
  ThreadDepth = 25
  ThreadDepthType = 0
  ThreadDirection = 0
  ThreadFit = 0
  ThreadSize = 0
  ThreadType = 0
  Threaded = false
  UseCustomThreadClearance = false
  expr: Diameter = <<Monitor Chassis Parameters>>.GSTowerLayerJoinScrewDiameter
  expr: HoleCutDiameter = <<Monitor Chassis Parameters>>.GSM2BoltCountersinkDiameter
FEATURE [Part::Part2DObjectPython] ShapeString  label="Direction and ID ShapeString"  # Draft 2D object (typed FeaturePython)
  FontFile = <path>
  Fuse = false
  Justification = 6
  JustificationReference = 0
  KeepLeftMargin = false
  MakeFace = true
  ObliqueAngle = 0
  Placement = pos=(46.66,-0.3,5.22) rot=(0.57735,-0.57735,0.57735;2.0944rad)
  ScaleToSize = true
  Size = 5
  String = PiTrac                --> UP                                               --> UP
  Tracking = 0
FEATURE [PartDesign::Pocket] Pocket004  label="Direction and ID Pocket"
  BaseFeature = -> Hole002
  Direction = (1e-16,1,-2e-16)
  Length = 1
  Length2 = 5
  Placement = pos=(0,0,0) rot=(1,0,0;1.5708rad)
  Profile = -> ShapeString
  ReferenceAxis = -> ShapeString [N_Axis]
  Suppressed = false
  Type = 0
FEATURE [PartDesign::Body] Body  label="Backplate Body - Connector Board Variant"
  AllowCompound = false
  Group = -> [Sketch,Sketch001,Pad,Pad001,Sketch002,Pad002,Sketch003,Hole,DatumPlane,Sketch004,Pad003,Mirrored,DatumPlane007,Sketch017,Hole002,ShapeString,Pocket004]
  Origin = -> Origin001
  Placement = pos=(0.2,-1,0) rot=(0,0,1;0rad)
  Tip = -> Pocket004
FEATURE [App::Part] Part  label="Tower Part - Connector Board Variant"
  Group = -> [Body,Body001]
  Origin = -> Origin
note: 1 file-system path scrubbed to <path> (originals preserved in the JSON sidecar)
